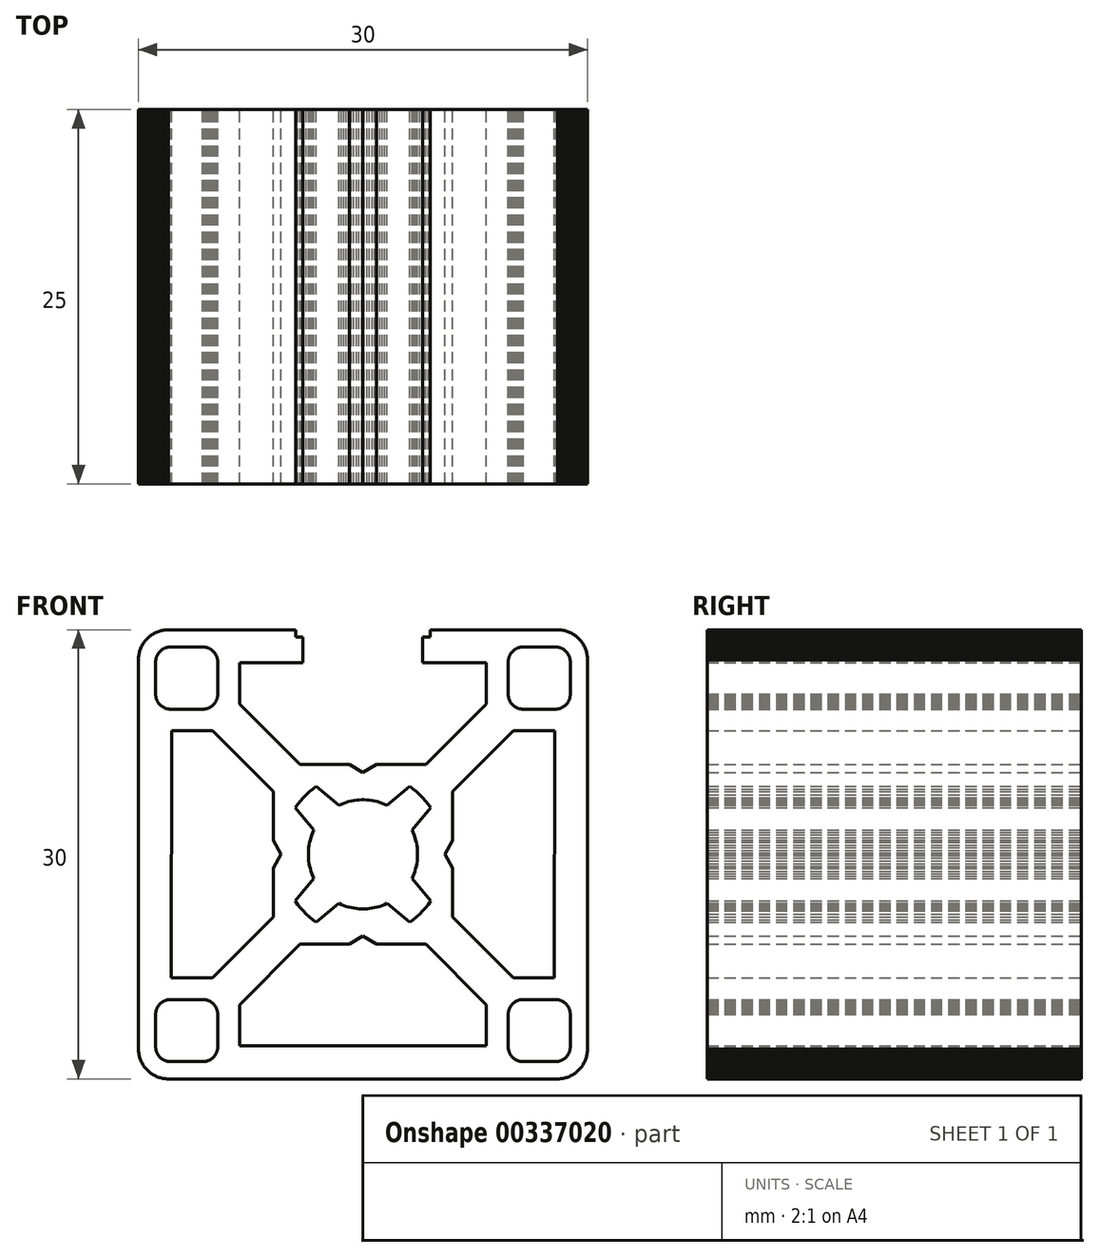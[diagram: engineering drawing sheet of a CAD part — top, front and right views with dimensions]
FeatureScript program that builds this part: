
annotation { "Feature Type Name" : "Feature", "Feature Type Description" : "" }
export const myFeature = defineFeature(function(context is Context, id is Id, definition is map)
    precondition{}
    {
        {
            var Q0;
            Q0=qCreatedBy(makeId("Front.planeOp"),FACE);
            var sketch = newSketch(context, id + "F0", { "sketchPlane" : qUnion([Q0])});
            skLineSegment(sketch, "E0", {"start": v(9.7, -12.9) * mm, "end": v(9.7, -12.85) * mm});
            skLineSegment(sketch, "E1", {"start": v(-13.85, -12.9) * mm, "end": v(-13.85, -12.85) * mm});
            skLineSegment(sketch, "E2", {"start": v(13.85, -10.7) * mm, "end": v(13.85, -10.66) * mm});
            skLineSegment(sketch, "E3", {"start": v(-9.7, -10.7) * mm, "end": v(-9.7, -10.66) * mm});
            skLineSegment(sketch, "E4", {"start": v(9.7, 10.66) * mm, "end": v(9.7, 10.7) * mm});
            skLineSegment(sketch, "E5", {"start": v(-13.85, 10.66) * mm, "end": v(-13.85, 10.7) * mm});
            skLineSegment(sketch, "E6", {"start": v(13.85, 12.85) * mm, "end": v(13.85, 12.9) * mm});
            skLineSegment(sketch, "E7", {"start": v(-9.7, 12.85) * mm, "end": v(-9.7, 12.9) * mm});
            skLineSegment(sketch, "E8", {"start": v(-15, -13.09) * mm, "end": v(-15, -13) * mm});
            skLineSegment(sketch, "E9", {"start": v(15, 13) * mm, "end": v(15, 13.09) * mm});
            skLineSegment(sketch, "E10", {"start": v(-3.64, -0.26) * mm, "end": v(-3.65, -0.09) * mm});
            skLineSegment(sketch, "E11", {"start": v(3.65, 0.09) * mm, "end": v(3.64, 0.26) * mm});
            skLineSegment(sketch, "E12", {"start": v(9.7, -12.94) * mm, "end": v(9.7, -12.9) * mm});
            skLineSegment(sketch, "E13", {"start": v(-9.7, -10.66) * mm, "end": v(-9.7, -10.61) * mm});
            skLineSegment(sketch, "E14", {"start": v(9.7, 10.61) * mm, "end": v(9.7, 10.66) * mm});
            skLineSegment(sketch, "E15", {"start": v(-9.7, 12.9) * mm, "end": v(-9.7, 12.94) * mm});
            skLineSegment(sketch, "E16", {"start": v(-15, -13.18) * mm, "end": v(-15, -13.09) * mm});
            skLineSegment(sketch, "E17", {"start": v(15, 13.09) * mm, "end": v(15, 13.18) * mm});
            skLineSegment(sketch, "E18", {"start": v(-13.85, -12.94) * mm, "end": v(-13.85, -12.9) * mm});
            skLineSegment(sketch, "E19", {"start": v(13.85, -10.66) * mm, "end": v(13.85, -10.61) * mm});
            skLineSegment(sketch, "E20", {"start": v(-13.85, 10.61) * mm, "end": v(-13.85, 10.66) * mm});
            skLineSegment(sketch, "E21", {"start": v(13.85, 12.9) * mm, "end": v(13.85, 12.94) * mm});
            skLineSegment(sketch, "E22", {"start": v(-3.62, -0.44) * mm, "end": v(-3.64, -0.26) * mm});
            skLineSegment(sketch, "E23", {"start": v(3.64, 0.26) * mm, "end": v(3.62, 0.44) * mm});
            skLineSegment(sketch, "E24", {"start": v(13.85, -10.61) * mm, "end": v(13.84, -10.57) * mm});
            skLineSegment(sketch, "E25", {"start": v(-13.84, 10.57) * mm, "end": v(-13.85, 10.61) * mm});
            skLineSegment(sketch, "E26", {"start": v(-13.84, -12.98) * mm, "end": v(-13.85, -12.94) * mm});
            skLineSegment(sketch, "E27", {"start": v(13.85, 12.94) * mm, "end": v(13.84, 12.98) * mm});
            skLineSegment(sketch, "E28", {"start": v(-14.98, -13.27) * mm, "end": v(-15, -13.18) * mm});
            skLineSegment(sketch, "E29", {"start": v(15, 13.18) * mm, "end": v(14.98, 13.27) * mm});
            skLineSegment(sketch, "E30", {"start": v(-9.7, -10.61) * mm, "end": v(-9.7, -10.57) * mm});
            skLineSegment(sketch, "E31", {"start": v(9.7, 10.57) * mm, "end": v(9.7, 10.61) * mm});
            skLineSegment(sketch, "E32", {"start": v(9.7, -12.98) * mm, "end": v(9.7, -12.94) * mm});
            skLineSegment(sketch, "E33", {"start": v(-9.7, 12.94) * mm, "end": v(-9.7, 12.98) * mm});
            skLineSegment(sketch, "E34", {"start": v(-3.6, -0.61) * mm, "end": v(-3.62, -0.44) * mm});
            skLineSegment(sketch, "E35", {"start": v(3.62, 0.44) * mm, "end": v(3.6, 0.61) * mm});
            skLineSegment(sketch, "E36", {"start": v(9.72, -13.03) * mm, "end": v(9.7, -12.98) * mm});
            skLineSegment(sketch, "E37", {"start": v(-13.83, -13.03) * mm, "end": v(-13.84, -12.98) * mm});
            skLineSegment(sketch, "E38", {"start": v(13.84, 12.98) * mm, "end": v(13.83, 13.03) * mm});
            skLineSegment(sketch, "E39", {"start": v(-9.7, 12.98) * mm, "end": v(-9.72, 13.03) * mm});
            skLineSegment(sketch, "E40", {"start": v(-14.97, -13.36) * mm, "end": v(-14.98, -13.27) * mm});
            skLineSegment(sketch, "E41", {"start": v(14.98, 13.27) * mm, "end": v(14.97, 13.36) * mm});
            skLineSegment(sketch, "E42", {"start": v(13.84, -10.57) * mm, "end": v(13.83, -10.52) * mm});
            skLineSegment(sketch, "E43", {"start": v(-9.7, -10.57) * mm, "end": v(-9.72, -10.52) * mm});
            skLineSegment(sketch, "E44", {"start": v(9.72, 10.52) * mm, "end": v(9.7, 10.57) * mm});
            skLineSegment(sketch, "E45", {"start": v(-13.83, 10.52) * mm, "end": v(-13.84, 10.57) * mm});
            skLineSegment(sketch, "E46", {"start": v(-3.56, -0.79) * mm, "end": v(-3.6, -0.61) * mm});
            skLineSegment(sketch, "E47", {"start": v(3.6, 0.61) * mm, "end": v(3.56, 0.79) * mm});
            skLineSegment(sketch, "E48", {"start": v(-14.95, -13.45) * mm, "end": v(-14.97, -13.36) * mm});
            skLineSegment(sketch, "E49", {"start": v(14.97, 13.36) * mm, "end": v(14.95, 13.45) * mm});
            skLineSegment(sketch, "E50", {"start": v(9.73, -13.07) * mm, "end": v(9.72, -13.03) * mm});
            skLineSegment(sketch, "E51", {"start": v(-13.82, -13.07) * mm, "end": v(-13.83, -13.03) * mm});
            skLineSegment(sketch, "E52", {"start": v(13.83, -10.52) * mm, "end": v(13.82, -10.48) * mm});
            skLineSegment(sketch, "E53", {"start": v(-9.72, -10.52) * mm, "end": v(-9.73, -10.48) * mm});
            skLineSegment(sketch, "E54", {"start": v(9.73, 10.48) * mm, "end": v(9.72, 10.52) * mm});
            skLineSegment(sketch, "E55", {"start": v(-13.82, 10.48) * mm, "end": v(-13.83, 10.52) * mm});
            skLineSegment(sketch, "E56", {"start": v(13.83, 13.03) * mm, "end": v(13.82, 13.07) * mm});
            skLineSegment(sketch, "E57", {"start": v(-9.72, 13.03) * mm, "end": v(-9.73, 13.07) * mm});
            skLineSegment(sketch, "E58", {"start": v(-3.52, -0.96) * mm, "end": v(-3.56, -0.79) * mm});
            skLineSegment(sketch, "E59", {"start": v(3.56, 0.79) * mm, "end": v(3.52, 0.96) * mm});
            skLineSegment(sketch, "E60", {"start": v(-14.93, -13.53) * mm, "end": v(-14.95, -13.45) * mm});
            skLineSegment(sketch, "E61", {"start": v(13.82, -10.48) * mm, "end": v(13.81, -10.43) * mm});
            skLineSegment(sketch, "E62", {"start": v(-9.73, -10.48) * mm, "end": v(-9.74, -10.43) * mm});
            skLineSegment(sketch, "E63", {"start": v(9.74, 10.43) * mm, "end": v(9.73, 10.48) * mm});
            skLineSegment(sketch, "E64", {"start": v(-13.81, 10.43) * mm, "end": v(-13.82, 10.48) * mm});
            skLineSegment(sketch, "E65", {"start": v(14.95, 13.45) * mm, "end": v(14.93, 13.53) * mm});
            skLineSegment(sketch, "E66", {"start": v(9.74, -13.12) * mm, "end": v(9.73, -13.07) * mm});
            skLineSegment(sketch, "E67", {"start": v(-13.81, -13.12) * mm, "end": v(-13.82, -13.07) * mm});
            skLineSegment(sketch, "E68", {"start": v(13.82, 13.07) * mm, "end": v(13.81, 13.12) * mm});
            skLineSegment(sketch, "E69", {"start": v(-9.73, 13.07) * mm, "end": v(-9.74, 13.12) * mm});
            skLineSegment(sketch, "E70", {"start": v(-3.47, -1.13) * mm, "end": v(-3.52, -0.96) * mm});
            skLineSegment(sketch, "E71", {"start": v(3.52, 0.96) * mm, "end": v(3.47, 1.13) * mm});
            skLineSegment(sketch, "E72", {"start": v(9.75, -13.16) * mm, "end": v(9.74, -13.12) * mm});
            skLineSegment(sketch, "E73", {"start": v(-13.8, -13.16) * mm, "end": v(-13.81, -13.12) * mm});
            skLineSegment(sketch, "E74", {"start": v(13.81, 13.12) * mm, "end": v(13.8, 13.16) * mm});
            skLineSegment(sketch, "E75", {"start": v(-9.74, 13.12) * mm, "end": v(-9.75, 13.16) * mm});
            skLineSegment(sketch, "E76", {"start": v(13.81, -10.43) * mm, "end": v(13.8, -10.4) * mm});
            skLineSegment(sketch, "E77", {"start": v(-9.74, -10.43) * mm, "end": v(-9.75, -10.4) * mm});
            skLineSegment(sketch, "E78", {"start": v(9.75, 10.4) * mm, "end": v(9.74, 10.43) * mm});
            skLineSegment(sketch, "E79", {"start": v(-13.8, 10.4) * mm, "end": v(-13.81, 10.43) * mm});
            skLineSegment(sketch, "E80", {"start": v(-14.9, -13.62) * mm, "end": v(-14.93, -13.53) * mm});
            skLineSegment(sketch, "E81", {"start": v(14.93, 13.53) * mm, "end": v(14.9, 13.62) * mm});
            skLineSegment(sketch, "E82", {"start": v(-14.87, -13.7) * mm, "end": v(-14.9, -13.62) * mm});
            skLineSegment(sketch, "E83", {"start": v(14.9, 13.62) * mm, "end": v(14.87, 13.7) * mm});
            skLineSegment(sketch, "E84", {"start": v(9.76, -13.2) * mm, "end": v(9.75, -13.16) * mm});
            skLineSegment(sketch, "E85", {"start": v(-13.79, -13.2) * mm, "end": v(-13.8, -13.16) * mm});
            skLineSegment(sketch, "E86", {"start": v(13.8, -10.4) * mm, "end": v(13.79, -10.35) * mm});
            skLineSegment(sketch, "E87", {"start": v(-9.75, -10.4) * mm, "end": v(-9.76, -10.35) * mm});
            skLineSegment(sketch, "E88", {"start": v(9.76, 10.35) * mm, "end": v(9.75, 10.4) * mm});
            skLineSegment(sketch, "E89", {"start": v(-13.79, 10.35) * mm, "end": v(-13.8, 10.4) * mm});
            skLineSegment(sketch, "E90", {"start": v(13.8, 13.16) * mm, "end": v(13.79, 13.2) * mm});
            skLineSegment(sketch, "E91", {"start": v(-9.75, 13.16) * mm, "end": v(-9.76, 13.2) * mm});
            skLineSegment(sketch, "E92", {"start": v(-3.41, -1.3) * mm, "end": v(-3.47, -1.13) * mm});
            skLineSegment(sketch, "E93", {"start": v(3.47, 1.13) * mm, "end": v(3.41, 1.3) * mm});
            skLineSegment(sketch, "E94", {"start": v(-14.84, -13.79) * mm, "end": v(-14.87, -13.7) * mm});
            skLineSegment(sketch, "E95", {"start": v(14.87, 13.7) * mm, "end": v(14.84, 13.79) * mm});
            skLineSegment(sketch, "E96", {"start": v(9.78, -13.24) * mm, "end": v(9.76, -13.2) * mm});
            skLineSegment(sketch, "E97", {"start": v(-9.76, -10.35) * mm, "end": v(-9.78, -10.3) * mm});
            skLineSegment(sketch, "E98", {"start": v(9.78, 10.3) * mm, "end": v(9.76, 10.35) * mm});
            skLineSegment(sketch, "E99", {"start": v(-9.76, 13.2) * mm, "end": v(-9.78, 13.24) * mm});
            skLineSegment(sketch, "E100", {"start": v(-13.77, -13.24) * mm, "end": v(-13.79, -13.2) * mm});
            skLineSegment(sketch, "E101", {"start": v(13.79, -10.35) * mm, "end": v(13.77, -10.3) * mm});
            skLineSegment(sketch, "E102", {"start": v(-13.77, 10.3) * mm, "end": v(-13.79, 10.35) * mm});
            skLineSegment(sketch, "E103", {"start": v(13.79, 13.2) * mm, "end": v(13.77, 13.24) * mm});
            skLineSegment(sketch, "E104", {"start": v(-3.35, -1.46) * mm, "end": v(-3.41, -1.3) * mm});
            skLineSegment(sketch, "E105", {"start": v(3.41, 1.3) * mm, "end": v(3.35, 1.46) * mm});
            skLineSegment(sketch, "E106", {"start": v(-13.75, -13.28) * mm, "end": v(-13.77, -13.24) * mm});
            skLineSegment(sketch, "E107", {"start": v(13.77, -10.3) * mm, "end": v(13.75, -10.27) * mm});
            skLineSegment(sketch, "E108", {"start": v(-13.75, 10.27) * mm, "end": v(-13.77, 10.3) * mm});
            skLineSegment(sketch, "E109", {"start": v(13.77, 13.24) * mm, "end": v(13.75, 13.28) * mm});
            skLineSegment(sketch, "E110", {"start": v(9.8, -13.28) * mm, "end": v(9.78, -13.24) * mm});
            skLineSegment(sketch, "E111", {"start": v(-9.78, -10.3) * mm, "end": v(-9.8, -10.27) * mm});
            skLineSegment(sketch, "E112", {"start": v(9.8, 10.27) * mm, "end": v(9.78, 10.3) * mm});
            skLineSegment(sketch, "E113", {"start": v(-9.78, 13.24) * mm, "end": v(-9.8, 13.28) * mm});
            skLineSegment(sketch, "E114", {"start": v(-14.8, -13.87) * mm, "end": v(-14.84, -13.79) * mm});
            skLineSegment(sketch, "E115", {"start": v(14.84, 13.79) * mm, "end": v(14.8, 13.87) * mm});
            skLineSegment(sketch, "E116", {"start": v(-3.27, -1.62) * mm, "end": v(-3.35, -1.46) * mm});
            skLineSegment(sketch, "E117", {"start": v(3.35, 1.46) * mm, "end": v(3.27, 1.62) * mm});
            skLineSegment(sketch, "E118", {"start": v(-13.73, -13.32) * mm, "end": v(-13.75, -13.28) * mm});
            skLineSegment(sketch, "E119", {"start": v(13.75, -10.27) * mm, "end": v(13.73, -10.23) * mm});
            skLineSegment(sketch, "E120", {"start": v(-13.73, 10.23) * mm, "end": v(-13.75, 10.27) * mm});
            skLineSegment(sketch, "E121", {"start": v(13.75, 13.28) * mm, "end": v(13.73, 13.32) * mm});
            skLineSegment(sketch, "E122", {"start": v(-14.76, -13.95) * mm, "end": v(-14.8, -13.87) * mm});
            skLineSegment(sketch, "E123", {"start": v(14.8, 13.87) * mm, "end": v(14.76, 13.95) * mm});
            skLineSegment(sketch, "E124", {"start": v(9.82, -13.32) * mm, "end": v(9.8, -13.28) * mm});
            skLineSegment(sketch, "E125", {"start": v(-9.8, -10.27) * mm, "end": v(-9.82, -10.23) * mm});
            skLineSegment(sketch, "E126", {"start": v(9.82, 10.23) * mm, "end": v(9.8, 10.27) * mm});
            skLineSegment(sketch, "E127", {"start": v(-9.8, 13.28) * mm, "end": v(-9.82, 13.32) * mm});
            skLineSegment(sketch, "E128", {"start": v(-9.82, -10.23) * mm, "end": v(-9.84, -10.19) * mm});
            skLineSegment(sketch, "E129", {"start": v(9.84, 10.19) * mm, "end": v(9.82, 10.23) * mm});
            skLineSegment(sketch, "E130", {"start": v(9.84, -13.36) * mm, "end": v(9.82, -13.32) * mm});
            skLineSegment(sketch, "E131", {"start": v(-9.82, 13.32) * mm, "end": v(-9.84, 13.36) * mm});
            skLineSegment(sketch, "E132", {"start": v(-14.72, -14.03) * mm, "end": v(-14.76, -13.95) * mm});
            skLineSegment(sketch, "E133", {"start": v(14.76, 13.95) * mm, "end": v(14.72, 14.03) * mm});
            skLineSegment(sketch, "E134", {"start": v(13.73, -10.23) * mm, "end": v(13.7, -10.19) * mm});
            skLineSegment(sketch, "E135", {"start": v(-13.7, 10.19) * mm, "end": v(-13.73, 10.23) * mm});
            skLineSegment(sketch, "E136", {"start": v(-13.7, -13.36) * mm, "end": v(-13.73, -13.32) * mm});
            skLineSegment(sketch, "E137", {"start": v(13.73, 13.32) * mm, "end": v(13.7, 13.36) * mm});
            skLineSegment(sketch, "E138", {"start": v(6, -0.92) * mm, "end": v(5.47, 0) * mm});
            skLineSegment(sketch, "E139", {"start": v(-5.47, 0) * mm, "end": v(-6, 0.92) * mm});
            skLineSegment(sketch, "E140", {"start": v(-13.68, -13.4) * mm, "end": v(-13.7, -13.36) * mm});
            skLineSegment(sketch, "E141", {"start": v(13.7, 13.36) * mm, "end": v(13.68, 13.4) * mm});
            skLineSegment(sketch, "E142", {"start": v(13.7, -10.19) * mm, "end": v(13.68, -10.15) * mm});
            skLineSegment(sketch, "E143", {"start": v(-13.68, 10.15) * mm, "end": v(-13.7, 10.19) * mm});
            skLineSegment(sketch, "E144", {"start": v(-14.67, -14.1) * mm, "end": v(-14.72, -14.03) * mm});
            skLineSegment(sketch, "E145", {"start": v(14.72, 14.03) * mm, "end": v(14.67, 14.1) * mm});
            skLineSegment(sketch, "E146", {"start": v(9.87, -13.4) * mm, "end": v(9.84, -13.36) * mm});
            skLineSegment(sketch, "E147", {"start": v(-9.84, 13.36) * mm, "end": v(-9.87, 13.4) * mm});
            skLineSegment(sketch, "E148", {"start": v(-9.84, -10.19) * mm, "end": v(-9.87, -10.15) * mm});
            skLineSegment(sketch, "E149", {"start": v(9.87, 10.15) * mm, "end": v(9.84, 10.19) * mm});
            skLineSegment(sketch, "E150", {"start": v(9.9, -13.44) * mm, "end": v(9.87, -13.4) * mm});
            skLineSegment(sketch, "E151", {"start": v(-13.66, -13.44) * mm, "end": v(-13.68, -13.4) * mm});
            skLineSegment(sketch, "E152", {"start": v(13.68, -10.15) * mm, "end": v(13.66, -10.11) * mm});
            skLineSegment(sketch, "E153", {"start": v(-9.87, -10.15) * mm, "end": v(-9.9, -10.11) * mm});
            skLineSegment(sketch, "E154", {"start": v(9.9, 10.11) * mm, "end": v(9.87, 10.15) * mm});
            skLineSegment(sketch, "E155", {"start": v(-13.66, 10.11) * mm, "end": v(-13.68, 10.15) * mm});
            skLineSegment(sketch, "E156", {"start": v(13.68, 13.4) * mm, "end": v(13.66, 13.44) * mm});
            skLineSegment(sketch, "E157", {"start": v(-9.87, 13.4) * mm, "end": v(-9.9, 13.44) * mm});
            skLineSegment(sketch, "E158", {"start": v(-14.62, -14.18) * mm, "end": v(-14.67, -14.1) * mm});
            skLineSegment(sketch, "E159", {"start": v(14.67, 14.1) * mm, "end": v(14.62, 14.18) * mm});
            skLineSegment(sketch, "E160", {"start": v(-4.36, -3.35) * mm, "end": v(-4.53, -3.12) * mm});
            skLineSegment(sketch, "E161", {"start": v(4.53, 3.12) * mm, "end": v(4.36, 3.35) * mm});
            skLineSegment(sketch, "E162", {"start": v(9.92, -13.47) * mm, "end": v(9.9, -13.44) * mm});
            skLineSegment(sketch, "E163", {"start": v(-9.9, -10.11) * mm, "end": v(-9.92, -10.08) * mm});
            skLineSegment(sketch, "E164", {"start": v(9.92, 10.08) * mm, "end": v(9.9, 10.11) * mm});
            skLineSegment(sketch, "E165", {"start": v(-9.9, 13.44) * mm, "end": v(-9.92, 13.47) * mm});
            skLineSegment(sketch, "E166", {"start": v(-14.56, -14.25) * mm, "end": v(-14.62, -14.18) * mm});
            skLineSegment(sketch, "E167", {"start": v(14.62, 14.18) * mm, "end": v(14.56, 14.25) * mm});
            skLineSegment(sketch, "E168", {"start": v(-13.63, -13.47) * mm, "end": v(-13.66, -13.44) * mm});
            skLineSegment(sketch, "E169", {"start": v(13.66, -10.11) * mm, "end": v(13.63, -10.08) * mm});
            skLineSegment(sketch, "E170", {"start": v(-13.63, 10.08) * mm, "end": v(-13.66, 10.11) * mm});
            skLineSegment(sketch, "E171", {"start": v(13.66, 13.44) * mm, "end": v(13.63, 13.47) * mm});
            skLineSegment(sketch, "E172", {"start": v(-4.18, -3.57) * mm, "end": v(-4.36, -3.35) * mm});
            skLineSegment(sketch, "E173", {"start": v(4.36, 3.35) * mm, "end": v(4.18, 3.57) * mm});
            skLineSegment(sketch, "E174", {"start": v(-14.5, -14.32) * mm, "end": v(-14.56, -14.25) * mm});
            skLineSegment(sketch, "E175", {"start": v(13.63, -10.08) * mm, "end": v(13.6, -10.04) * mm});
            skLineSegment(sketch, "E176", {"start": v(-13.6, 10.04) * mm, "end": v(-13.63, 10.08) * mm});
            skLineSegment(sketch, "E177", {"start": v(14.56, 14.25) * mm, "end": v(14.5, 14.32) * mm});
            skLineSegment(sketch, "E178", {"start": v(-13.6, -13.5) * mm, "end": v(-13.63, -13.47) * mm});
            skLineSegment(sketch, "E179", {"start": v(13.63, 13.47) * mm, "end": v(13.6, 13.5) * mm});
            skLineSegment(sketch, "E180", {"start": v(-9.92, -10.08) * mm, "end": v(-9.95, -10.04) * mm});
            skLineSegment(sketch, "E181", {"start": v(9.95, 10.04) * mm, "end": v(9.92, 10.08) * mm});
            skLineSegment(sketch, "E182", {"start": v(9.95, -13.5) * mm, "end": v(9.92, -13.47) * mm});
            skLineSegment(sketch, "E183", {"start": v(-9.92, 13.47) * mm, "end": v(-9.95, 13.5) * mm});
            skLineSegment(sketch, "E184", {"start": v(4.53, -3.12) * mm, "end": v(3.27, -1.62) * mm});
            skLineSegment(sketch, "E185", {"start": v(-3.27, 1.62) * mm, "end": v(-4.53, 3.12) * mm});
            skLineSegment(sketch, "E186", {"start": v(-3.99, -3.79) * mm, "end": v(-4.18, -3.57) * mm});
            skLineSegment(sketch, "E187", {"start": v(4.18, 3.57) * mm, "end": v(3.99, 3.79) * mm});
            skLineSegment(sketch, "E188", {"start": v(9.98, -13.54) * mm, "end": v(9.95, -13.5) * mm});
            skLineSegment(sketch, "E189", {"start": v(-13.57, -13.54) * mm, "end": v(-13.6, -13.5) * mm});
            skLineSegment(sketch, "E190", {"start": v(13.6, -10.04) * mm, "end": v(13.57, -10) * mm});
            skLineSegment(sketch, "E191", {"start": v(-9.95, -10.04) * mm, "end": v(-9.98, -10) * mm});
            skLineSegment(sketch, "E192", {"start": v(9.98, 10) * mm, "end": v(9.95, 10.04) * mm});
            skLineSegment(sketch, "E193", {"start": v(-13.57, 10) * mm, "end": v(-13.6, 10.04) * mm});
            skLineSegment(sketch, "E194", {"start": v(13.6, 13.5) * mm, "end": v(13.57, 13.54) * mm});
            skLineSegment(sketch, "E195", {"start": v(-9.95, 13.5) * mm, "end": v(-9.98, 13.54) * mm});
            skLineSegment(sketch, "E196", {"start": v(-14.45, -14.38) * mm, "end": v(-14.5, -14.32) * mm});
            skLineSegment(sketch, "E197", {"start": v(14.5, 14.32) * mm, "end": v(14.45, 14.38) * mm});
            skLineSegment(sketch, "E198", {"start": v(10, -13.57) * mm, "end": v(9.98, -13.54) * mm});
            skLineSegment(sketch, "E199", {"start": v(-9.98, 13.54) * mm, "end": v(-10, 13.57) * mm});
            skLineSegment(sketch, "E200", {"start": v(-14.38, -14.45) * mm, "end": v(-14.45, -14.38) * mm});
            skLineSegment(sketch, "E201", {"start": v(-13.54, -13.57) * mm, "end": v(-13.57, -13.54) * mm});
            skLineSegment(sketch, "E202", {"start": v(8.25, -10.05) * mm, "end": v(4.2, -6) * mm});
            skLineSegment(sketch, "E203", {"start": v(-9.98, -10) * mm, "end": v(-10, -9.98) * mm});
            skLineSegment(sketch, "E204", {"start": v(-3.79, -3.99) * mm, "end": v(-3.99, -3.79) * mm});
            skLineSegment(sketch, "E205", {"start": v(3.99, 3.79) * mm, "end": v(3.79, 3.99) * mm});
            skLineSegment(sketch, "E206", {"start": v(-6, 4.2) * mm, "end": v(-10.05, 8.25) * mm});
            skLineSegment(sketch, "E207", {"start": v(-4.2, 6) * mm, "end": v(-8.25, 10.05) * mm});
            skLineSegment(sketch, "E208", {"start": v(10.05, -8.25) * mm, "end": v(6, -4.2) * mm});
            skLineSegment(sketch, "E209", {"start": v(10, 9.98) * mm, "end": v(9.98, 10) * mm});
            skLineSegment(sketch, "E210", {"start": v(13.57, 13.54) * mm, "end": v(13.54, 13.57) * mm});
            skLineSegment(sketch, "E211", {"start": v(14.45, 14.38) * mm, "end": v(14.38, 14.45) * mm});
            skLineSegment(sketch, "E212", {"start": v(13.57, -10) * mm, "end": v(13.54, -9.98) * mm});
            skLineSegment(sketch, "E213", {"start": v(-13.54, 9.98) * mm, "end": v(-13.57, 10) * mm});
            skLineSegment(sketch, "E214", {"start": v(-14.32, -14.5) * mm, "end": v(-14.38, -14.45) * mm});
            skLineSegment(sketch, "E215", {"start": v(14.38, 14.45) * mm, "end": v(14.32, 14.5) * mm});
            skLineSegment(sketch, "E216", {"start": v(10.04, -13.6) * mm, "end": v(10, -13.57) * mm});
            skLineSegment(sketch, "E217", {"start": v(-13.5, -13.6) * mm, "end": v(-13.54, -13.57) * mm});
            skLineSegment(sketch, "E218", {"start": v(13.54, -9.98) * mm, "end": v(13.5, -9.95) * mm});
            skLineSegment(sketch, "E219", {"start": v(-10, -9.98) * mm, "end": v(-10.04, -9.95) * mm});
            skLineSegment(sketch, "E220", {"start": v(10.04, 9.95) * mm, "end": v(10, 9.98) * mm});
            skLineSegment(sketch, "E221", {"start": v(-13.5, 9.95) * mm, "end": v(-13.54, 9.98) * mm});
            skLineSegment(sketch, "E222", {"start": v(13.54, 13.57) * mm, "end": v(13.5, 13.6) * mm});
            skLineSegment(sketch, "E223", {"start": v(-10, 13.57) * mm, "end": v(-10.04, 13.6) * mm});
            skLineSegment(sketch, "E224", {"start": v(-3.57, -4.18) * mm, "end": v(-3.79, -3.99) * mm});
            skLineSegment(sketch, "E225", {"start": v(3.79, 3.99) * mm, "end": v(3.57, 4.18) * mm});
            skLineSegment(sketch, "E226", {"start": v(3.12, -4.53) * mm, "end": v(1.62, -3.27) * mm});
            skLineSegment(sketch, "E227", {"start": v(-1.62, 3.27) * mm, "end": v(-3.12, 4.53) * mm});
            skLineSegment(sketch, "E228", {"start": v(13.5, -9.95) * mm, "end": v(13.47, -9.92) * mm});
            skLineSegment(sketch, "E229", {"start": v(-13.47, 9.92) * mm, "end": v(-13.5, 9.95) * mm});
            skLineSegment(sketch, "E230", {"start": v(-10.04, -9.95) * mm, "end": v(-10.08, -9.92) * mm});
            skLineSegment(sketch, "E231", {"start": v(10.08, 9.92) * mm, "end": v(10.04, 9.95) * mm});
            skLineSegment(sketch, "E232", {"start": v(-13.47, -13.63) * mm, "end": v(-13.5, -13.6) * mm});
            skLineSegment(sketch, "E233", {"start": v(13.5, 13.6) * mm, "end": v(13.47, 13.63) * mm});
            skLineSegment(sketch, "E234", {"start": v(-14.25, -14.56) * mm, "end": v(-14.32, -14.5) * mm});
            skLineSegment(sketch, "E235", {"start": v(10.08, -13.63) * mm, "end": v(10.04, -13.6) * mm});
            skLineSegment(sketch, "E236", {"start": v(-10.04, 13.6) * mm, "end": v(-10.08, 13.63) * mm});
            skLineSegment(sketch, "E237", {"start": v(14.32, 14.5) * mm, "end": v(14.25, 14.56) * mm});
            skLineSegment(sketch, "E238", {"start": v(-3.35, -4.36) * mm, "end": v(-3.57, -4.18) * mm});
            skLineSegment(sketch, "E239", {"start": v(3.57, 4.18) * mm, "end": v(3.35, 4.36) * mm});
            skLineSegment(sketch, "E240", {"start": v(10.11, -13.66) * mm, "end": v(10.08, -13.63) * mm});
            skLineSegment(sketch, "E241", {"start": v(-13.44, -13.66) * mm, "end": v(-13.47, -13.63) * mm});
            skLineSegment(sketch, "E242", {"start": v(13.47, 13.63) * mm, "end": v(13.44, 13.66) * mm});
            skLineSegment(sketch, "E243", {"start": v(-10.08, 13.63) * mm, "end": v(-10.11, 13.66) * mm});
            skLineSegment(sketch, "E244", {"start": v(-14.18, -14.62) * mm, "end": v(-14.25, -14.56) * mm});
            skLineSegment(sketch, "E245", {"start": v(14.25, 14.56) * mm, "end": v(14.18, 14.62) * mm});
            skLineSegment(sketch, "E246", {"start": v(13.47, -9.92) * mm, "end": v(13.44, -9.9) * mm});
            skLineSegment(sketch, "E247", {"start": v(-10.08, -9.92) * mm, "end": v(-10.11, -9.9) * mm});
            skLineSegment(sketch, "E248", {"start": v(10.11, 9.9) * mm, "end": v(10.08, 9.92) * mm});
            skLineSegment(sketch, "E249", {"start": v(-13.44, 9.9) * mm, "end": v(-13.47, 9.92) * mm});
            skLineSegment(sketch, "E250", {"start": v(-3.12, -4.53) * mm, "end": v(-3.35, -4.36) * mm});
            skLineSegment(sketch, "E251", {"start": v(3.35, 4.36) * mm, "end": v(3.12, 4.53) * mm});
            skLineSegment(sketch, "E252", {"start": v(-14.1, -14.67) * mm, "end": v(-14.18, -14.62) * mm});
            skLineSegment(sketch, "E253", {"start": v(14.18, 14.62) * mm, "end": v(14.1, 14.67) * mm});
            skLineSegment(sketch, "E254", {"start": v(10.15, -13.68) * mm, "end": v(10.11, -13.66) * mm});
            skLineSegment(sketch, "E255", {"start": v(-13.4, -13.68) * mm, "end": v(-13.44, -13.66) * mm});
            skLineSegment(sketch, "E256", {"start": v(13.44, -9.9) * mm, "end": v(13.4, -9.87) * mm});
            skLineSegment(sketch, "E257", {"start": v(-10.11, -9.9) * mm, "end": v(-10.15, -9.87) * mm});
            skLineSegment(sketch, "E258", {"start": v(10.15, 9.87) * mm, "end": v(10.11, 9.9) * mm});
            skLineSegment(sketch, "E259", {"start": v(-13.4, 9.87) * mm, "end": v(-13.44, 9.9) * mm});
            skLineSegment(sketch, "E260", {"start": v(13.44, 13.66) * mm, "end": v(13.4, 13.68) * mm});
            skLineSegment(sketch, "E261", {"start": v(-10.11, 13.66) * mm, "end": v(-10.15, 13.68) * mm});
            skLineSegment(sketch, "E262", {"start": v(-10.15, -9.87) * mm, "end": v(-10.19, -9.84) * mm});
            skLineSegment(sketch, "E263", {"start": v(10.19, 9.84) * mm, "end": v(10.15, 9.87) * mm});
            skLineSegment(sketch, "E264", {"start": v(13.4, -9.87) * mm, "end": v(13.36, -9.84) * mm});
            skLineSegment(sketch, "E265", {"start": v(-13.36, 9.84) * mm, "end": v(-13.4, 9.87) * mm});
            skLineSegment(sketch, "E266", {"start": v(-14.03, -14.72) * mm, "end": v(-14.1, -14.67) * mm});
            skLineSegment(sketch, "E267", {"start": v(14.1, 14.67) * mm, "end": v(14.03, 14.72) * mm});
            skLineSegment(sketch, "E268", {"start": v(10.19, -13.7) * mm, "end": v(10.15, -13.68) * mm});
            skLineSegment(sketch, "E269", {"start": v(-10.15, 13.68) * mm, "end": v(-10.19, 13.7) * mm});
            skLineSegment(sketch, "E270", {"start": v(-13.36, -13.7) * mm, "end": v(-13.4, -13.68) * mm});
            skLineSegment(sketch, "E271", {"start": v(13.4, 13.68) * mm, "end": v(13.36, 13.7) * mm});
            skLineSegment(sketch, "E272", {"start": v(0.92, -6) * mm, "end": v(0, -5.47) * mm});
            skLineSegment(sketch, "E273", {"start": v(0, 5.47) * mm, "end": v(-0.92, 6) * mm});
            skLineSegment(sketch, "E274", {"start": v(-13.32, -13.73) * mm, "end": v(-13.36, -13.7) * mm});
            skLineSegment(sketch, "E275", {"start": v(13.36, 13.7) * mm, "end": v(13.32, 13.73) * mm});
            skLineSegment(sketch, "E276", {"start": v(10.23, -13.73) * mm, "end": v(10.19, -13.7) * mm});
            skLineSegment(sketch, "E277", {"start": v(-10.19, 13.7) * mm, "end": v(-10.23, 13.73) * mm});
            skLineSegment(sketch, "E278", {"start": v(-13.95, -14.76) * mm, "end": v(-14.03, -14.72) * mm});
            skLineSegment(sketch, "E279", {"start": v(14.03, 14.72) * mm, "end": v(13.95, 14.76) * mm});
            skLineSegment(sketch, "E280", {"start": v(13.36, -9.84) * mm, "end": v(13.32, -9.82) * mm});
            skLineSegment(sketch, "E281", {"start": v(-13.32, 9.82) * mm, "end": v(-13.36, 9.84) * mm});
            skLineSegment(sketch, "E282", {"start": v(-10.19, -9.84) * mm, "end": v(-10.23, -9.82) * mm});
            skLineSegment(sketch, "E283", {"start": v(10.23, 9.82) * mm, "end": v(10.19, 9.84) * mm});
            skLineSegment(sketch, "E284", {"start": v(13.32, -9.82) * mm, "end": v(13.28, -9.8) * mm});
            skLineSegment(sketch, "E285", {"start": v(-10.23, -9.82) * mm, "end": v(-10.27, -9.8) * mm});
            skLineSegment(sketch, "E286", {"start": v(10.27, 9.8) * mm, "end": v(10.23, 9.82) * mm});
            skLineSegment(sketch, "E287", {"start": v(-13.28, 9.8) * mm, "end": v(-13.32, 9.82) * mm});
            skLineSegment(sketch, "E288", {"start": v(-13.87, -14.8) * mm, "end": v(-13.95, -14.76) * mm});
            skLineSegment(sketch, "E289", {"start": v(13.95, 14.76) * mm, "end": v(13.87, 14.8) * mm});
            skLineSegment(sketch, "E290", {"start": v(10.27, -13.75) * mm, "end": v(10.23, -13.73) * mm});
            skLineSegment(sketch, "E291", {"start": v(-13.28, -13.75) * mm, "end": v(-13.32, -13.73) * mm});
            skLineSegment(sketch, "E292", {"start": v(13.32, 13.73) * mm, "end": v(13.28, 13.75) * mm});
            skLineSegment(sketch, "E293", {"start": v(-10.23, 13.73) * mm, "end": v(-10.27, 13.75) * mm});
            skLineSegment(sketch, "E294", {"start": v(-1.46, -3.35) * mm, "end": v(-1.62, -3.27) * mm});
            skLineSegment(sketch, "E295", {"start": v(1.62, 3.27) * mm, "end": v(1.46, 3.35) * mm});
            skLineSegment(sketch, "E296", {"start": v(-13.79, -14.84) * mm, "end": v(-13.87, -14.8) * mm});
            skLineSegment(sketch, "E297", {"start": v(13.87, 14.8) * mm, "end": v(13.79, 14.84) * mm});
            skLineSegment(sketch, "E298", {"start": v(13.28, -9.8) * mm, "end": v(13.24, -9.78) * mm});
            skLineSegment(sketch, "E299", {"start": v(-10.27, -9.8) * mm, "end": v(-10.3, -9.78) * mm});
            skLineSegment(sketch, "E300", {"start": v(10.3, 9.78) * mm, "end": v(10.27, 9.8) * mm});
            skLineSegment(sketch, "E301", {"start": v(-13.24, 9.78) * mm, "end": v(-13.28, 9.8) * mm});
            skLineSegment(sketch, "E302", {"start": v(10.3, -13.77) * mm, "end": v(10.27, -13.75) * mm});
            skLineSegment(sketch, "E303", {"start": v(-13.24, -13.77) * mm, "end": v(-13.28, -13.75) * mm});
            skLineSegment(sketch, "E304", {"start": v(13.28, 13.75) * mm, "end": v(13.24, 13.77) * mm});
            skLineSegment(sketch, "E305", {"start": v(-10.27, 13.75) * mm, "end": v(-10.3, 13.77) * mm});
            skLineSegment(sketch, "E306", {"start": v(-1.3, -3.41) * mm, "end": v(-1.46, -3.35) * mm});
            skLineSegment(sketch, "E307", {"start": v(1.46, 3.35) * mm, "end": v(1.3, 3.41) * mm});
            skLineSegment(sketch, "E308", {"start": v(10.35, -13.79) * mm, "end": v(10.3, -13.77) * mm});
            skLineSegment(sketch, "E309", {"start": v(-13.2, -13.79) * mm, "end": v(-13.24, -13.77) * mm});
            skLineSegment(sketch, "E310", {"start": v(13.24, 13.77) * mm, "end": v(13.2, 13.79) * mm});
            skLineSegment(sketch, "E311", {"start": v(-10.3, 13.77) * mm, "end": v(-10.35, 13.79) * mm});
            skLineSegment(sketch, "E312", {"start": v(13.24, -9.78) * mm, "end": v(13.2, -9.76) * mm});
            skLineSegment(sketch, "E313", {"start": v(-10.3, -9.78) * mm, "end": v(-10.35, -9.76) * mm});
            skLineSegment(sketch, "E314", {"start": v(10.35, 9.76) * mm, "end": v(10.3, 9.78) * mm});
            skLineSegment(sketch, "E315", {"start": v(-13.2, 9.76) * mm, "end": v(-13.24, 9.78) * mm});
            skLineSegment(sketch, "E316", {"start": v(-13.7, -14.87) * mm, "end": v(-13.79, -14.84) * mm});
            skLineSegment(sketch, "E317", {"start": v(13.79, 14.84) * mm, "end": v(13.7, 14.87) * mm});
            skLineSegment(sketch, "E318", {"start": v(-1.13, -3.47) * mm, "end": v(-1.3, -3.41) * mm});
            skLineSegment(sketch, "E319", {"start": v(1.3, 3.41) * mm, "end": v(1.13, 3.47) * mm});
            skLineSegment(sketch, "E320", {"start": v(10.4, -13.8) * mm, "end": v(10.35, -13.79) * mm});
            skLineSegment(sketch, "E321", {"start": v(-13.16, -13.8) * mm, "end": v(-13.2, -13.79) * mm});
            skLineSegment(sketch, "E322", {"start": v(13.2, -9.76) * mm, "end": v(13.16, -9.75) * mm});
            skLineSegment(sketch, "E323", {"start": v(-10.35, -9.76) * mm, "end": v(-10.4, -9.75) * mm});
            skLineSegment(sketch, "E324", {"start": v(10.4, 9.75) * mm, "end": v(10.35, 9.76) * mm});
            skLineSegment(sketch, "E325", {"start": v(-13.16, 9.75) * mm, "end": v(-13.2, 9.76) * mm});
            skLineSegment(sketch, "E326", {"start": v(13.2, 13.79) * mm, "end": v(13.16, 13.8) * mm});
            skLineSegment(sketch, "E327", {"start": v(-10.35, 13.79) * mm, "end": v(-10.4, 13.8) * mm});
            skLineSegment(sketch, "E328", {"start": v(-13.62, -14.9) * mm, "end": v(-13.7, -14.87) * mm});
            skLineSegment(sketch, "E329", {"start": v(13.7, 14.87) * mm, "end": v(13.62, 14.9) * mm});
            skLineSegment(sketch, "E330", {"start": v(-13.53, -14.93) * mm, "end": v(-13.62, -14.9) * mm});
            skLineSegment(sketch, "E331", {"start": v(13.62, 14.9) * mm, "end": v(13.53, 14.93) * mm});
            skLineSegment(sketch, "E332", {"start": v(10.43, -13.81) * mm, "end": v(10.4, -13.8) * mm});
            skLineSegment(sketch, "E333", {"start": v(-10.4, -9.75) * mm, "end": v(-10.43, -9.74) * mm});
            skLineSegment(sketch, "E334", {"start": v(10.43, 9.74) * mm, "end": v(10.4, 9.75) * mm});
            skLineSegment(sketch, "E335", {"start": v(-10.4, 13.8) * mm, "end": v(-10.43, 13.81) * mm});
            skLineSegment(sketch, "E336", {"start": v(-13.12, -13.81) * mm, "end": v(-13.16, -13.8) * mm});
            skLineSegment(sketch, "E337", {"start": v(13.16, -9.75) * mm, "end": v(13.12, -9.74) * mm});
            skLineSegment(sketch, "E338", {"start": v(-13.12, 9.74) * mm, "end": v(-13.16, 9.75) * mm});
            skLineSegment(sketch, "E339", {"start": v(13.16, 13.8) * mm, "end": v(13.12, 13.81) * mm});
            skLineSegment(sketch, "E340", {"start": v(-0.96, -3.52) * mm, "end": v(-1.13, -3.47) * mm});
            skLineSegment(sketch, "E341", {"start": v(1.13, 3.47) * mm, "end": v(0.96, 3.52) * mm});
            skLineSegment(sketch, "E342", {"start": v(-13.07, -13.82) * mm, "end": v(-13.12, -13.81) * mm});
            skLineSegment(sketch, "E343", {"start": v(13.12, -9.74) * mm, "end": v(13.07, -9.73) * mm});
            skLineSegment(sketch, "E344", {"start": v(-13.07, 9.73) * mm, "end": v(-13.12, 9.74) * mm});
            skLineSegment(sketch, "E345", {"start": v(13.12, 13.81) * mm, "end": v(13.07, 13.82) * mm});
            skLineSegment(sketch, "E346", {"start": v(-13.45, -14.95) * mm, "end": v(-13.53, -14.93) * mm});
            skLineSegment(sketch, "E347", {"start": v(10.48, -13.82) * mm, "end": v(10.43, -13.81) * mm});
            skLineSegment(sketch, "E348", {"start": v(-10.43, -9.74) * mm, "end": v(-10.48, -9.73) * mm});
            skLineSegment(sketch, "E349", {"start": v(10.48, 9.73) * mm, "end": v(10.43, 9.74) * mm});
            skLineSegment(sketch, "E350", {"start": v(-10.43, 13.81) * mm, "end": v(-10.48, 13.82) * mm});
            skLineSegment(sketch, "E351", {"start": v(13.53, 14.93) * mm, "end": v(13.45, 14.95) * mm});
            skLineSegment(sketch, "E352", {"start": v(-0.79, -3.56) * mm, "end": v(-0.96, -3.52) * mm});
            skLineSegment(sketch, "E353", {"start": v(0.96, 3.52) * mm, "end": v(0.79, 3.56) * mm});
            skLineSegment(sketch, "E354", {"start": v(10.52, -13.83) * mm, "end": v(10.48, -13.82) * mm});
            skLineSegment(sketch, "E355", {"start": v(-13.03, -13.83) * mm, "end": v(-13.07, -13.82) * mm});
            skLineSegment(sketch, "E356", {"start": v(13.07, -9.73) * mm, "end": v(13.03, -9.72) * mm});
            skLineSegment(sketch, "E357", {"start": v(-10.48, -9.73) * mm, "end": v(-10.52, -9.72) * mm});
            skLineSegment(sketch, "E358", {"start": v(10.52, 9.72) * mm, "end": v(10.48, 9.73) * mm});
            skLineSegment(sketch, "E359", {"start": v(-13.03, 9.72) * mm, "end": v(-13.07, 9.73) * mm});
            skLineSegment(sketch, "E360", {"start": v(13.07, 13.82) * mm, "end": v(13.03, 13.83) * mm});
            skLineSegment(sketch, "E361", {"start": v(-10.48, 13.82) * mm, "end": v(-10.52, 13.83) * mm});
            skLineSegment(sketch, "E362", {"start": v(-13.36, -14.97) * mm, "end": v(-13.45, -14.95) * mm});
            skLineSegment(sketch, "E363", {"start": v(13.45, 14.95) * mm, "end": v(13.36, 14.97) * mm});
            skLineSegment(sketch, "E364", {"start": v(-0.61, -3.6) * mm, "end": v(-0.79, -3.56) * mm});
            skLineSegment(sketch, "E365", {"start": v(0.79, 3.56) * mm, "end": v(0.61, 3.6) * mm});
            skLineSegment(sketch, "E366", {"start": v(10.57, -13.84) * mm, "end": v(10.52, -13.83) * mm});
            skLineSegment(sketch, "E367", {"start": v(-10.52, -9.72) * mm, "end": v(-10.57, -9.7) * mm});
            skLineSegment(sketch, "E368", {"start": v(10.57, 9.7) * mm, "end": v(10.52, 9.72) * mm});
            skLineSegment(sketch, "E369", {"start": v(-10.52, 13.83) * mm, "end": v(-10.57, 13.84) * mm});
            skLineSegment(sketch, "E370", {"start": v(-13.27, -14.98) * mm, "end": v(-13.36, -14.97) * mm});
            skLineSegment(sketch, "E371", {"start": v(13.36, 14.97) * mm, "end": v(13.27, 14.98) * mm});
            skLineSegment(sketch, "E372", {"start": v(-12.98, -13.84) * mm, "end": v(-13.03, -13.83) * mm});
            skLineSegment(sketch, "E373", {"start": v(13.03, -9.72) * mm, "end": v(12.98, -9.7) * mm});
            skLineSegment(sketch, "E374", {"start": v(-12.98, 9.7) * mm, "end": v(-13.03, 9.72) * mm});
            skLineSegment(sketch, "E375", {"start": v(13.03, 13.83) * mm, "end": v(12.98, 13.84) * mm});
            skLineSegment(sketch, "E376", {"start": v(-0.44, -3.62) * mm, "end": v(-0.61, -3.6) * mm});
            skLineSegment(sketch, "E377", {"start": v(0.61, 3.6) * mm, "end": v(0.44, 3.62) * mm});
            skLineSegment(sketch, "E378", {"start": v(12.98, -9.7) * mm, "end": v(12.94, -9.7) * mm});
            skLineSegment(sketch, "E379", {"start": v(-12.94, 9.7) * mm, "end": v(-12.98, 9.7) * mm});
            skLineSegment(sketch, "E380", {"start": v(-10.57, -9.7) * mm, "end": v(-10.61, -9.7) * mm});
            skLineSegment(sketch, "E381", {"start": v(10.61, 9.7) * mm, "end": v(10.57, 9.7) * mm});
            skLineSegment(sketch, "E382", {"start": v(-13.18, -15) * mm, "end": v(-13.27, -14.98) * mm});
            skLineSegment(sketch, "E383", {"start": v(13.27, 14.98) * mm, "end": v(13.18, 15) * mm});
            skLineSegment(sketch, "E384", {"start": v(-12.94, -13.85) * mm, "end": v(-12.98, -13.84) * mm});
            skLineSegment(sketch, "E385", {"start": v(12.98, 13.84) * mm, "end": v(12.94, 13.85) * mm});
            skLineSegment(sketch, "E386", {"start": v(10.61, -13.85) * mm, "end": v(10.57, -13.84) * mm});
            skLineSegment(sketch, "E387", {"start": v(-10.57, 13.84) * mm, "end": v(-10.61, 13.85) * mm});
            skLineSegment(sketch, "E388", {"start": v(-0.26, -3.64) * mm, "end": v(-0.44, -3.62) * mm});
            skLineSegment(sketch, "E389", {"start": v(0.44, 3.62) * mm, "end": v(0.26, 3.64) * mm});
            skLineSegment(sketch, "E390", {"start": v(-13.09, -15) * mm, "end": v(-13.18, -15) * mm});
            skLineSegment(sketch, "E391", {"start": v(10.66, -13.85) * mm, "end": v(10.61, -13.85) * mm});
            skLineSegment(sketch, "E392", {"start": v(-12.9, -13.85) * mm, "end": v(-12.94, -13.85) * mm});
            skLineSegment(sketch, "E393", {"start": v(12.94, 13.85) * mm, "end": v(12.9, 13.85) * mm});
            skLineSegment(sketch, "E394", {"start": v(-10.61, 13.85) * mm, "end": v(-10.66, 13.85) * mm});
            skLineSegment(sketch, "E395", {"start": v(13.18, 15) * mm, "end": v(13.09, 15) * mm});
            skLineSegment(sketch, "E396", {"start": v(12.94, -9.7) * mm, "end": v(12.9, -9.7) * mm});
            skLineSegment(sketch, "E397", {"start": v(-10.61, -9.7) * mm, "end": v(-10.66, -9.7) * mm});
            skLineSegment(sketch, "E398", {"start": v(10.66, 9.7) * mm, "end": v(10.61, 9.7) * mm});
            skLineSegment(sketch, "E399", {"start": v(-12.9, 9.7) * mm, "end": v(-12.94, 9.7) * mm});
            skLineSegment(sketch, "E400", {"start": v(-0.09, -3.65) * mm, "end": v(-0.26, -3.64) * mm});
            skLineSegment(sketch, "E401", {"start": v(0.26, 3.64) * mm, "end": v(0.09, 3.65) * mm});
            skLineSegment(sketch, "E402", {"start": v(-13, -15) * mm, "end": v(-13.09, -15) * mm});
            skLineSegment(sketch, "E403", {"start": v(10.7, -13.85) * mm, "end": v(10.66, -13.85) * mm});
            skLineSegment(sketch, "E404", {"start": v(-12.85, -13.85) * mm, "end": v(-12.9, -13.85) * mm});
            skLineSegment(sketch, "E405", {"start": v(12.9, -9.7) * mm, "end": v(12.85, -9.7) * mm});
            skLineSegment(sketch, "E406", {"start": v(-10.66, -9.7) * mm, "end": v(-10.7, -9.7) * mm});
            skLineSegment(sketch, "E407", {"start": v(10.7, 9.7) * mm, "end": v(10.66, 9.7) * mm});
            skLineSegment(sketch, "E408", {"start": v(-12.85, 9.7) * mm, "end": v(-12.9, 9.7) * mm});
            skLineSegment(sketch, "E409", {"start": v(12.9, 13.85) * mm, "end": v(12.85, 13.85) * mm});
            skLineSegment(sketch, "E410", {"start": v(-10.66, 13.85) * mm, "end": v(-10.7, 13.85) * mm});
            skLineSegment(sketch, "E411", {"start": v(13.09, 15) * mm, "end": v(13, 15) * mm});
            skLineSegment(sketch, "E412", {"start": v(8.25, -12.8) * mm, "end": v(-8.25, -12.8) * mm});
            skLineSegment(sketch, "E413", {"start": v(-4, 12.8) * mm, "end": v(-8.25, 12.8) * mm});
            skLineSegment(sketch, "E414", {"start": v(-13, -15) * mm, "end": v(13, -15) * mm});
            skLineSegment(sketch, "E415", {"start": v(10.7, -13.85) * mm, "end": v(12.85, -13.85) * mm});
            skLineSegment(sketch, "E416", {"start": v(-12.85, -13.85) * mm, "end": v(-10.7, -13.85) * mm});
            skLineSegment(sketch, "E417", {"start": v(10.7, -9.7) * mm, "end": v(12.85, -9.7) * mm});
            skLineSegment(sketch, "E418", {"start": v(-12.85, -9.7) * mm, "end": v(-10.7, -9.7) * mm});
            skLineSegment(sketch, "E419", {"start": v(10.05, -8.25) * mm, "end": v(12.8, -8.25) * mm});
            skLineSegment(sketch, "E420", {"start": v(-12.8, -8.25) * mm, "end": v(-10.05, -8.25) * mm});
            skLineSegment(sketch, "E421", {"start": v(0.92, -6) * mm, "end": v(4.2, -6) * mm});
            skLineSegment(sketch, "E422", {"start": v(-4.2, -6) * mm, "end": v(-0.92, -6) * mm});
            skLineSegment(sketch, "E423", {"start": v(-0.09, -3.65) * mm, "end": v(0.09, -3.65) * mm});
            skLineSegment(sketch, "E424", {"start": v(-0.09, 3.65) * mm, "end": v(0.09, 3.65) * mm});
            skLineSegment(sketch, "E425", {"start": v(0.92, 6) * mm, "end": v(4.2, 6) * mm});
            skLineSegment(sketch, "E426", {"start": v(-4.2, 6) * mm, "end": v(-0.92, 6) * mm});
            skLineSegment(sketch, "E427", {"start": v(10.05, 8.25) * mm, "end": v(12.8, 8.25) * mm});
            skLineSegment(sketch, "E428", {"start": v(-12.8, 8.25) * mm, "end": v(-10.05, 8.25) * mm});
            skLineSegment(sketch, "E429", {"start": v(10.7, 9.7) * mm, "end": v(12.85, 9.7) * mm});
            skLineSegment(sketch, "E430", {"start": v(-12.85, 9.7) * mm, "end": v(-10.7, 9.7) * mm});
            skLineSegment(sketch, "E431", {"start": v(10.7, 13.85) * mm, "end": v(12.85, 13.85) * mm});
            skLineSegment(sketch, "E432", {"start": v(-12.85, 13.85) * mm, "end": v(-10.7, 13.85) * mm});
            skLineSegment(sketch, "E433", {"start": v(-4.5, 14.5) * mm, "end": v(-4, 14.5) * mm});
            skLineSegment(sketch, "E434", {"start": v(4, 14.5) * mm, "end": v(4.5, 14.5) * mm});
            skLineSegment(sketch, "E435", {"start": v(-13, 15) * mm, "end": v(-4.5, 15) * mm});
            skLineSegment(sketch, "E436", {"start": v(4.5, 15) * mm, "end": v(13, 15) * mm});
            skLineSegment(sketch, "E437", {"start": v(4, 12.8) * mm, "end": v(8.25, 12.8) * mm});
            skLineSegment(sketch, "E438", {"start": v(13, -15) * mm, "end": v(13.09, -15) * mm});
            skLineSegment(sketch, "E439", {"start": v(12.85, -13.85) * mm, "end": v(12.9, -13.85) * mm});
            skLineSegment(sketch, "E440", {"start": v(-10.7, -13.85) * mm, "end": v(-10.66, -13.85) * mm});
            skLineSegment(sketch, "E441", {"start": v(10.66, -9.7) * mm, "end": v(10.7, -9.7) * mm});
            skLineSegment(sketch, "E442", {"start": v(-12.9, -9.7) * mm, "end": v(-12.85, -9.7) * mm});
            skLineSegment(sketch, "E443", {"start": v(12.85, 9.7) * mm, "end": v(12.9, 9.7) * mm});
            skLineSegment(sketch, "E444", {"start": v(-10.7, 9.7) * mm, "end": v(-10.66, 9.7) * mm});
            skLineSegment(sketch, "E445", {"start": v(10.66, 13.85) * mm, "end": v(10.7, 13.85) * mm});
            skLineSegment(sketch, "E446", {"start": v(-12.9, 13.85) * mm, "end": v(-12.85, 13.85) * mm});
            skLineSegment(sketch, "E447", {"start": v(-13.09, 15) * mm, "end": v(-13, 15) * mm});
            skLineSegment(sketch, "E448", {"start": v(0.09, -3.65) * mm, "end": v(0.26, -3.64) * mm});
            skLineSegment(sketch, "E449", {"start": v(-0.26, 3.64) * mm, "end": v(-0.09, 3.65) * mm});
            skLineSegment(sketch, "E450", {"start": v(10.61, -9.7) * mm, "end": v(10.66, -9.7) * mm});
            skLineSegment(sketch, "E451", {"start": v(-12.94, -9.7) * mm, "end": v(-12.9, -9.7) * mm});
            skLineSegment(sketch, "E452", {"start": v(12.9, 9.7) * mm, "end": v(12.94, 9.7) * mm});
            skLineSegment(sketch, "E453", {"start": v(-10.66, 9.7) * mm, "end": v(-10.61, 9.7) * mm});
            skLineSegment(sketch, "E454", {"start": v(13.09, -15) * mm, "end": v(13.18, -15) * mm});
            skLineSegment(sketch, "E455", {"start": v(12.9, -13.85) * mm, "end": v(12.94, -13.85) * mm});
            skLineSegment(sketch, "E456", {"start": v(-10.66, -13.85) * mm, "end": v(-10.61, -13.85) * mm});
            skLineSegment(sketch, "E457", {"start": v(10.61, 13.85) * mm, "end": v(10.66, 13.85) * mm});
            skLineSegment(sketch, "E458", {"start": v(-12.94, 13.85) * mm, "end": v(-12.9, 13.85) * mm});
            skLineSegment(sketch, "E459", {"start": v(-13.18, 15) * mm, "end": v(-13.09, 15) * mm});
            skLineSegment(sketch, "E460", {"start": v(0.26, -3.64) * mm, "end": v(0.44, -3.62) * mm});
            skLineSegment(sketch, "E461", {"start": v(-0.44, 3.62) * mm, "end": v(-0.26, 3.64) * mm});
            skLineSegment(sketch, "E462", {"start": v(-10.61, -13.85) * mm, "end": v(-10.57, -13.84) * mm});
            skLineSegment(sketch, "E463", {"start": v(10.57, 13.84) * mm, "end": v(10.61, 13.85) * mm});
            skLineSegment(sketch, "E464", {"start": v(12.94, -13.85) * mm, "end": v(12.98, -13.84) * mm});
            skLineSegment(sketch, "E465", {"start": v(-12.98, 13.84) * mm, "end": v(-12.94, 13.85) * mm});
            skLineSegment(sketch, "E466", {"start": v(13.18, -15) * mm, "end": v(13.27, -14.98) * mm});
            skLineSegment(sketch, "E467", {"start": v(-13.27, 14.98) * mm, "end": v(-13.18, 15) * mm});
            skLineSegment(sketch, "E468", {"start": v(10.57, -9.7) * mm, "end": v(10.61, -9.7) * mm});
            skLineSegment(sketch, "E469", {"start": v(-10.61, 9.7) * mm, "end": v(-10.57, 9.7) * mm});
            skLineSegment(sketch, "E470", {"start": v(-12.98, -9.7) * mm, "end": v(-12.94, -9.7) * mm});
            skLineSegment(sketch, "E471", {"start": v(12.94, 9.7) * mm, "end": v(12.98, 9.7) * mm});
            skLineSegment(sketch, "E472", {"start": v(0.44, -3.62) * mm, "end": v(0.61, -3.6) * mm});
            skLineSegment(sketch, "E473", {"start": v(-0.61, 3.6) * mm, "end": v(-0.44, 3.62) * mm});
            skLineSegment(sketch, "E474", {"start": v(12.98, -13.84) * mm, "end": v(13.03, -13.83) * mm});
            skLineSegment(sketch, "E475", {"start": v(-13.03, -9.72) * mm, "end": v(-12.98, -9.7) * mm});
            skLineSegment(sketch, "E476", {"start": v(12.98, 9.7) * mm, "end": v(13.03, 9.72) * mm});
            skLineSegment(sketch, "E477", {"start": v(-13.03, 13.83) * mm, "end": v(-12.98, 13.84) * mm});
            skLineSegment(sketch, "E478", {"start": v(13.27, -14.98) * mm, "end": v(13.36, -14.97) * mm});
            skLineSegment(sketch, "E479", {"start": v(-13.36, 14.97) * mm, "end": v(-13.27, 14.98) * mm});
            skLineSegment(sketch, "E480", {"start": v(-10.57, -13.84) * mm, "end": v(-10.52, -13.83) * mm});
            skLineSegment(sketch, "E481", {"start": v(10.52, -9.72) * mm, "end": v(10.57, -9.7) * mm});
            skLineSegment(sketch, "E482", {"start": v(-10.57, 9.7) * mm, "end": v(-10.52, 9.72) * mm});
            skLineSegment(sketch, "E483", {"start": v(10.52, 13.83) * mm, "end": v(10.57, 13.84) * mm});
            skLineSegment(sketch, "E484", {"start": v(0.61, -3.6) * mm, "end": v(0.79, -3.56) * mm});
            skLineSegment(sketch, "E485", {"start": v(-0.79, 3.56) * mm, "end": v(-0.61, 3.6) * mm});
            skLineSegment(sketch, "E486", {"start": v(13.36, -14.97) * mm, "end": v(13.45, -14.95) * mm});
            skLineSegment(sketch, "E487", {"start": v(-13.45, 14.95) * mm, "end": v(-13.36, 14.97) * mm});
            skLineSegment(sketch, "E488", {"start": v(13.03, -13.83) * mm, "end": v(13.07, -13.82) * mm});
            skLineSegment(sketch, "E489", {"start": v(-10.52, -13.83) * mm, "end": v(-10.48, -13.82) * mm});
            skLineSegment(sketch, "E490", {"start": v(10.48, -9.73) * mm, "end": v(10.52, -9.72) * mm});
            skLineSegment(sketch, "E491", {"start": v(-13.07, -9.73) * mm, "end": v(-13.03, -9.72) * mm});
            skLineSegment(sketch, "E492", {"start": v(13.03, 9.72) * mm, "end": v(13.07, 9.73) * mm});
            skLineSegment(sketch, "E493", {"start": v(-10.52, 9.72) * mm, "end": v(-10.48, 9.73) * mm});
            skLineSegment(sketch, "E494", {"start": v(10.48, 13.82) * mm, "end": v(10.52, 13.83) * mm});
            skLineSegment(sketch, "E495", {"start": v(-13.07, 13.82) * mm, "end": v(-13.03, 13.83) * mm});
            skLineSegment(sketch, "E496", {"start": v(0.79, -3.56) * mm, "end": v(0.96, -3.52) * mm});
            skLineSegment(sketch, "E497", {"start": v(-0.96, 3.52) * mm, "end": v(-0.79, 3.56) * mm});
            skLineSegment(sketch, "E498", {"start": v(13.45, -14.95) * mm, "end": v(13.53, -14.93) * mm});
            skLineSegment(sketch, "E499", {"start": v(-10.48, -13.82) * mm, "end": v(-10.43, -13.81) * mm});
            skLineSegment(sketch, "E500", {"start": v(10.43, -9.74) * mm, "end": v(10.48, -9.73) * mm});
            skLineSegment(sketch, "E501", {"start": v(-10.48, 9.73) * mm, "end": v(-10.43, 9.74) * mm});
            skLineSegment(sketch, "E502", {"start": v(10.43, 13.81) * mm, "end": v(10.48, 13.82) * mm});
            skLineSegment(sketch, "E503", {"start": v(-13.53, 14.93) * mm, "end": v(-13.45, 14.95) * mm});
            skLineSegment(sketch, "E504", {"start": v(13.07, -13.82) * mm, "end": v(13.12, -13.81) * mm});
            skLineSegment(sketch, "E505", {"start": v(-13.12, -9.74) * mm, "end": v(-13.07, -9.73) * mm});
            skLineSegment(sketch, "E506", {"start": v(13.07, 9.73) * mm, "end": v(13.12, 9.74) * mm});
            skLineSegment(sketch, "E507", {"start": v(-13.12, 13.81) * mm, "end": v(-13.07, 13.82) * mm});
            skLineSegment(sketch, "E508", {"start": v(0.96, -3.52) * mm, "end": v(1.13, -3.47) * mm});
            skLineSegment(sketch, "E509", {"start": v(-1.13, 3.47) * mm, "end": v(-0.96, 3.52) * mm});
            skLineSegment(sketch, "E510", {"start": v(13.12, -13.81) * mm, "end": v(13.16, -13.8) * mm});
            skLineSegment(sketch, "E511", {"start": v(-13.16, -9.75) * mm, "end": v(-13.12, -9.74) * mm});
            skLineSegment(sketch, "E512", {"start": v(13.12, 9.74) * mm, "end": v(13.16, 9.75) * mm});
            skLineSegment(sketch, "E513", {"start": v(-13.16, 13.8) * mm, "end": v(-13.12, 13.81) * mm});
            skLineSegment(sketch, "E514", {"start": v(-10.43, -13.81) * mm, "end": v(-10.4, -13.8) * mm});
            skLineSegment(sketch, "E515", {"start": v(10.4, -9.75) * mm, "end": v(10.43, -9.74) * mm});
            skLineSegment(sketch, "E516", {"start": v(-10.43, 9.74) * mm, "end": v(-10.4, 9.75) * mm});
            skLineSegment(sketch, "E517", {"start": v(10.4, 13.8) * mm, "end": v(10.43, 13.81) * mm});
            skLineSegment(sketch, "E518", {"start": v(13.53, -14.93) * mm, "end": v(13.62, -14.9) * mm});
            skLineSegment(sketch, "E519", {"start": v(-13.62, 14.9) * mm, "end": v(-13.53, 14.93) * mm});
            skLineSegment(sketch, "E520", {"start": v(13.62, -14.9) * mm, "end": v(13.7, -14.87) * mm});
            skLineSegment(sketch, "E521", {"start": v(-13.7, 14.87) * mm, "end": v(-13.62, 14.9) * mm});
            skLineSegment(sketch, "E522", {"start": v(13.16, -13.8) * mm, "end": v(13.2, -13.79) * mm});
            skLineSegment(sketch, "E523", {"start": v(-10.4, -13.8) * mm, "end": v(-10.35, -13.79) * mm});
            skLineSegment(sketch, "E524", {"start": v(10.35, -9.76) * mm, "end": v(10.4, -9.75) * mm});
            skLineSegment(sketch, "E525", {"start": v(-13.2, -9.76) * mm, "end": v(-13.16, -9.75) * mm});
            skLineSegment(sketch, "E526", {"start": v(13.16, 9.75) * mm, "end": v(13.2, 9.76) * mm});
            skLineSegment(sketch, "E527", {"start": v(-10.4, 9.75) * mm, "end": v(-10.35, 9.76) * mm});
            skLineSegment(sketch, "E528", {"start": v(10.35, 13.79) * mm, "end": v(10.4, 13.8) * mm});
            skLineSegment(sketch, "E529", {"start": v(-13.2, 13.79) * mm, "end": v(-13.16, 13.8) * mm});
            skLineSegment(sketch, "E530", {"start": v(1.13, -3.47) * mm, "end": v(1.3, -3.41) * mm});
            skLineSegment(sketch, "E531", {"start": v(-1.3, 3.41) * mm, "end": v(-1.13, 3.47) * mm});
            skLineSegment(sketch, "E532", {"start": v(13.7, -14.87) * mm, "end": v(13.79, -14.84) * mm});
            skLineSegment(sketch, "E533", {"start": v(-13.79, 14.84) * mm, "end": v(-13.7, 14.87) * mm});
            skLineSegment(sketch, "E534", {"start": v(10.3, -9.78) * mm, "end": v(10.35, -9.76) * mm});
            skLineSegment(sketch, "E535", {"start": v(-13.24, -9.78) * mm, "end": v(-13.2, -9.76) * mm});
            skLineSegment(sketch, "E536", {"start": v(13.2, 9.76) * mm, "end": v(13.24, 9.78) * mm});
            skLineSegment(sketch, "E537", {"start": v(-10.35, 9.76) * mm, "end": v(-10.3, 9.78) * mm});
            skLineSegment(sketch, "E538", {"start": v(13.2, -13.79) * mm, "end": v(13.24, -13.77) * mm});
            skLineSegment(sketch, "E539", {"start": v(-10.35, -13.79) * mm, "end": v(-10.3, -13.77) * mm});
            skLineSegment(sketch, "E540", {"start": v(10.3, 13.77) * mm, "end": v(10.35, 13.79) * mm});
            skLineSegment(sketch, "E541", {"start": v(-13.24, 13.77) * mm, "end": v(-13.2, 13.79) * mm});
            skLineSegment(sketch, "E542", {"start": v(1.3, -3.41) * mm, "end": v(1.46, -3.35) * mm});
            skLineSegment(sketch, "E543", {"start": v(-1.46, 3.35) * mm, "end": v(-1.3, 3.41) * mm});
            skLineSegment(sketch, "E544", {"start": v(13.24, -13.77) * mm, "end": v(13.28, -13.75) * mm});
            skLineSegment(sketch, "E545", {"start": v(-10.3, -13.77) * mm, "end": v(-10.27, -13.75) * mm});
            skLineSegment(sketch, "E546", {"start": v(10.27, 13.75) * mm, "end": v(10.3, 13.77) * mm});
            skLineSegment(sketch, "E547", {"start": v(-13.28, 13.75) * mm, "end": v(-13.24, 13.77) * mm});
            skLineSegment(sketch, "E548", {"start": v(10.27, -9.8) * mm, "end": v(10.3, -9.78) * mm});
            skLineSegment(sketch, "E549", {"start": v(-13.28, -9.8) * mm, "end": v(-13.24, -9.78) * mm});
            skLineSegment(sketch, "E550", {"start": v(13.24, 9.78) * mm, "end": v(13.28, 9.8) * mm});
            skLineSegment(sketch, "E551", {"start": v(-10.3, 9.78) * mm, "end": v(-10.27, 9.8) * mm});
            skLineSegment(sketch, "E552", {"start": v(13.79, -14.84) * mm, "end": v(13.87, -14.8) * mm});
            skLineSegment(sketch, "E553", {"start": v(-13.87, 14.8) * mm, "end": v(-13.79, 14.84) * mm});
            skLineSegment(sketch, "E554", {"start": v(1.46, -3.35) * mm, "end": v(1.62, -3.27) * mm});
            skLineSegment(sketch, "E555", {"start": v(-1.62, 3.27) * mm, "end": v(-1.46, 3.35) * mm});
            skLineSegment(sketch, "E556", {"start": v(13.28, -13.75) * mm, "end": v(13.32, -13.73) * mm});
            skLineSegment(sketch, "E557", {"start": v(-10.27, -13.75) * mm, "end": v(-10.23, -13.73) * mm});
            skLineSegment(sketch, "E558", {"start": v(10.23, 13.73) * mm, "end": v(10.27, 13.75) * mm});
            skLineSegment(sketch, "E559", {"start": v(-13.32, 13.73) * mm, "end": v(-13.28, 13.75) * mm});
            skLineSegment(sketch, "E560", {"start": v(13.87, -14.8) * mm, "end": v(13.95, -14.76) * mm});
            skLineSegment(sketch, "E561", {"start": v(-13.95, 14.76) * mm, "end": v(-13.87, 14.8) * mm});
            skLineSegment(sketch, "E562", {"start": v(10.23, -9.82) * mm, "end": v(10.27, -9.8) * mm});
            skLineSegment(sketch, "E563", {"start": v(-13.32, -9.82) * mm, "end": v(-13.28, -9.8) * mm});
            skLineSegment(sketch, "E564", {"start": v(13.28, 9.8) * mm, "end": v(13.32, 9.82) * mm});
            skLineSegment(sketch, "E565", {"start": v(-10.27, 9.8) * mm, "end": v(-10.23, 9.82) * mm});
            skLineSegment(sketch, "E566", {"start": v(10.19, -9.84) * mm, "end": v(10.23, -9.82) * mm});
            skLineSegment(sketch, "E567", {"start": v(-10.23, 9.82) * mm, "end": v(-10.19, 9.84) * mm});
            skLineSegment(sketch, "E568", {"start": v(-13.36, -9.84) * mm, "end": v(-13.32, -9.82) * mm});
            skLineSegment(sketch, "E569", {"start": v(13.32, 9.82) * mm, "end": v(13.36, 9.84) * mm});
            skLineSegment(sketch, "E570", {"start": v(13.95, -14.76) * mm, "end": v(14.03, -14.72) * mm});
            skLineSegment(sketch, "E571", {"start": v(-14.03, 14.72) * mm, "end": v(-13.95, 14.76) * mm});
            skLineSegment(sketch, "E572", {"start": v(-10.23, -13.73) * mm, "end": v(-10.19, -13.7) * mm});
            skLineSegment(sketch, "E573", {"start": v(10.19, 13.7) * mm, "end": v(10.23, 13.73) * mm});
            skLineSegment(sketch, "E574", {"start": v(13.32, -13.73) * mm, "end": v(13.36, -13.7) * mm});
            skLineSegment(sketch, "E575", {"start": v(-13.36, 13.7) * mm, "end": v(-13.32, 13.73) * mm});
            skLineSegment(sketch, "E576", {"start": v(-0.92, -6) * mm, "end": v(0, -5.47) * mm});
            skLineSegment(sketch, "E577", {"start": v(0, 5.47) * mm, "end": v(0.92, 6) * mm});
            skLineSegment(sketch, "E578", {"start": v(13.36, -13.7) * mm, "end": v(13.4, -13.68) * mm});
            skLineSegment(sketch, "E579", {"start": v(-13.4, 13.68) * mm, "end": v(-13.36, 13.7) * mm});
            skLineSegment(sketch, "E580", {"start": v(-10.19, -13.7) * mm, "end": v(-10.15, -13.68) * mm});
            skLineSegment(sketch, "E581", {"start": v(10.15, 13.68) * mm, "end": v(10.19, 13.7) * mm});
            skLineSegment(sketch, "E582", {"start": v(14.03, -14.72) * mm, "end": v(14.1, -14.67) * mm});
            skLineSegment(sketch, "E583", {"start": v(-14.1, 14.67) * mm, "end": v(-14.03, 14.72) * mm});
            skLineSegment(sketch, "E584", {"start": v(-13.4, -9.87) * mm, "end": v(-13.36, -9.84) * mm});
            skLineSegment(sketch, "E585", {"start": v(13.36, 9.84) * mm, "end": v(13.4, 9.87) * mm});
            skLineSegment(sketch, "E586", {"start": v(10.15, -9.87) * mm, "end": v(10.19, -9.84) * mm});
            skLineSegment(sketch, "E587", {"start": v(-10.19, 9.84) * mm, "end": v(-10.15, 9.87) * mm});
            skLineSegment(sketch, "E588", {"start": v(13.4, -13.68) * mm, "end": v(13.44, -13.66) * mm});
            skLineSegment(sketch, "E589", {"start": v(-10.15, -13.68) * mm, "end": v(-10.11, -13.66) * mm});
            skLineSegment(sketch, "E590", {"start": v(10.11, -9.9) * mm, "end": v(10.15, -9.87) * mm});
            skLineSegment(sketch, "E591", {"start": v(-13.44, -9.9) * mm, "end": v(-13.4, -9.87) * mm});
            skLineSegment(sketch, "E592", {"start": v(13.4, 9.87) * mm, "end": v(13.44, 9.9) * mm});
            skLineSegment(sketch, "E593", {"start": v(-10.15, 9.87) * mm, "end": v(-10.11, 9.9) * mm});
            skLineSegment(sketch, "E594", {"start": v(10.11, 13.66) * mm, "end": v(10.15, 13.68) * mm});
            skLineSegment(sketch, "E595", {"start": v(-13.44, 13.66) * mm, "end": v(-13.4, 13.68) * mm});
            skLineSegment(sketch, "E596", {"start": v(14.1, -14.67) * mm, "end": v(14.18, -14.62) * mm});
            skLineSegment(sketch, "E597", {"start": v(-14.18, 14.62) * mm, "end": v(-14.1, 14.67) * mm});
            skLineSegment(sketch, "E598", {"start": v(3.12, -4.53) * mm, "end": v(3.35, -4.36) * mm});
            skLineSegment(sketch, "E599", {"start": v(-3.35, 4.36) * mm, "end": v(-3.12, 4.53) * mm});
            skLineSegment(sketch, "E600", {"start": v(10.08, -9.92) * mm, "end": v(10.11, -9.9) * mm});
            skLineSegment(sketch, "E601", {"start": v(-13.47, -9.92) * mm, "end": v(-13.44, -9.9) * mm});
            skLineSegment(sketch, "E602", {"start": v(13.44, 9.9) * mm, "end": v(13.47, 9.92) * mm});
            skLineSegment(sketch, "E603", {"start": v(-10.11, 9.9) * mm, "end": v(-10.08, 9.92) * mm});
            skLineSegment(sketch, "E604", {"start": v(14.18, -14.62) * mm, "end": v(14.25, -14.56) * mm});
            skLineSegment(sketch, "E605", {"start": v(-14.25, 14.56) * mm, "end": v(-14.18, 14.62) * mm});
            skLineSegment(sketch, "E606", {"start": v(13.44, -13.66) * mm, "end": v(13.47, -13.63) * mm});
            skLineSegment(sketch, "E607", {"start": v(-10.11, -13.66) * mm, "end": v(-10.08, -13.63) * mm});
            skLineSegment(sketch, "E608", {"start": v(10.08, 13.63) * mm, "end": v(10.11, 13.66) * mm});
            skLineSegment(sketch, "E609", {"start": v(-13.47, 13.63) * mm, "end": v(-13.44, 13.66) * mm});
            skLineSegment(sketch, "E610", {"start": v(3.35, -4.36) * mm, "end": v(3.57, -4.18) * mm});
            skLineSegment(sketch, "E611", {"start": v(-3.57, 4.18) * mm, "end": v(-3.35, 4.36) * mm});
            skLineSegment(sketch, "E612", {"start": v(14.25, -14.56) * mm, "end": v(14.32, -14.5) * mm});
            skLineSegment(sketch, "E613", {"start": v(-10.08, -13.63) * mm, "end": v(-10.04, -13.6) * mm});
            skLineSegment(sketch, "E614", {"start": v(10.04, 13.6) * mm, "end": v(10.08, 13.63) * mm});
            skLineSegment(sketch, "E615", {"start": v(-14.32, 14.5) * mm, "end": v(-14.25, 14.56) * mm});
            skLineSegment(sketch, "E616", {"start": v(13.47, -13.63) * mm, "end": v(13.5, -13.6) * mm});
            skLineSegment(sketch, "E617", {"start": v(-13.5, 13.6) * mm, "end": v(-13.47, 13.63) * mm});
            skLineSegment(sketch, "E618", {"start": v(10.04, -9.95) * mm, "end": v(10.08, -9.92) * mm});
            skLineSegment(sketch, "E619", {"start": v(-10.08, 9.92) * mm, "end": v(-10.04, 9.95) * mm});
            skLineSegment(sketch, "E620", {"start": v(-13.5, -9.95) * mm, "end": v(-13.47, -9.92) * mm});
            skLineSegment(sketch, "E621", {"start": v(13.47, 9.92) * mm, "end": v(13.5, 9.95) * mm});
            skLineSegment(sketch, "E622", {"start": v(-3.12, -4.53) * mm, "end": v(-1.62, -3.27) * mm});
            skLineSegment(sketch, "E623", {"start": v(1.62, 3.27) * mm, "end": v(3.12, 4.53) * mm});
            skLineSegment(sketch, "E624", {"start": v(3.57, -4.18) * mm, "end": v(3.79, -3.99) * mm});
            skLineSegment(sketch, "E625", {"start": v(-3.79, 3.99) * mm, "end": v(-3.57, 4.18) * mm});
            skLineSegment(sketch, "E626", {"start": v(13.5, -13.6) * mm, "end": v(13.54, -13.57) * mm});
            skLineSegment(sketch, "E627", {"start": v(-10.04, -13.6) * mm, "end": v(-10, -13.57) * mm});
            skLineSegment(sketch, "E628", {"start": v(10, -9.98) * mm, "end": v(10.04, -9.95) * mm});
            skLineSegment(sketch, "E629", {"start": v(-13.54, -9.98) * mm, "end": v(-13.5, -9.95) * mm});
            skLineSegment(sketch, "E630", {"start": v(13.5, 9.95) * mm, "end": v(13.54, 9.98) * mm});
            skLineSegment(sketch, "E631", {"start": v(-10.04, 9.95) * mm, "end": v(-10, 9.98) * mm});
            skLineSegment(sketch, "E632", {"start": v(10, 13.57) * mm, "end": v(10.04, 13.6) * mm});
            skLineSegment(sketch, "E633", {"start": v(-13.54, 13.57) * mm, "end": v(-13.5, 13.6) * mm});
            skLineSegment(sketch, "E634", {"start": v(14.32, -14.5) * mm, "end": v(14.38, -14.45) * mm});
            skLineSegment(sketch, "E635", {"start": v(-14.38, 14.45) * mm, "end": v(-14.32, 14.5) * mm});
            skLineSegment(sketch, "E636", {"start": v(-13.57, -10) * mm, "end": v(-13.54, -9.98) * mm});
            skLineSegment(sketch, "E637", {"start": v(13.54, 9.98) * mm, "end": v(13.57, 10) * mm});
            skLineSegment(sketch, "E638", {"start": v(14.38, -14.45) * mm, "end": v(14.45, -14.38) * mm});
            skLineSegment(sketch, "E639", {"start": v(13.54, -13.57) * mm, "end": v(13.57, -13.54) * mm});
            skLineSegment(sketch, "E640", {"start": v(9.98, -10) * mm, "end": v(10, -9.98) * mm});
            skLineSegment(sketch, "E641", {"start": v(-10.05, -8.25) * mm, "end": v(-6, -4.2) * mm});
            skLineSegment(sketch, "E642", {"start": v(3.79, -3.99) * mm, "end": v(3.99, -3.79) * mm});
            skLineSegment(sketch, "E643", {"start": v(-3.99, 3.79) * mm, "end": v(-3.79, 3.99) * mm});
            skLineSegment(sketch, "E644", {"start": v(6, 4.2) * mm, "end": v(10.05, 8.25) * mm});
            skLineSegment(sketch, "E645", {"start": v(-8.25, -10.05) * mm, "end": v(-4.2, -6) * mm});
            skLineSegment(sketch, "E646", {"start": v(4.2, 6) * mm, "end": v(8.25, 10.05) * mm});
            skLineSegment(sketch, "E647", {"start": v(-10, 9.98) * mm, "end": v(-9.98, 10) * mm});
            skLineSegment(sketch, "E648", {"start": v(-13.57, 13.54) * mm, "end": v(-13.54, 13.57) * mm});
            skLineSegment(sketch, "E649", {"start": v(-14.45, 14.38) * mm, "end": v(-14.38, 14.45) * mm});
            skLineSegment(sketch, "E650", {"start": v(-10, -13.57) * mm, "end": v(-9.98, -13.54) * mm});
            skLineSegment(sketch, "E651", {"start": v(9.98, 13.54) * mm, "end": v(10, 13.57) * mm});
            skLineSegment(sketch, "E652", {"start": v(14.45, -14.38) * mm, "end": v(14.5, -14.32) * mm});
            skLineSegment(sketch, "E653", {"start": v(-14.5, 14.32) * mm, "end": v(-14.45, 14.38) * mm});
            skLineSegment(sketch, "E654", {"start": v(13.57, -13.54) * mm, "end": v(13.6, -13.5) * mm});
            skLineSegment(sketch, "E655", {"start": v(-9.98, -13.54) * mm, "end": v(-9.95, -13.5) * mm});
            skLineSegment(sketch, "E656", {"start": v(9.95, -10.04) * mm, "end": v(9.98, -10) * mm});
            skLineSegment(sketch, "E657", {"start": v(-13.6, -10.04) * mm, "end": v(-13.57, -10) * mm});
            skLineSegment(sketch, "E658", {"start": v(13.57, 10) * mm, "end": v(13.6, 10.04) * mm});
            skLineSegment(sketch, "E659", {"start": v(-9.98, 10) * mm, "end": v(-9.95, 10.04) * mm});
            skLineSegment(sketch, "E660", {"start": v(9.95, 13.5) * mm, "end": v(9.98, 13.54) * mm});
            skLineSegment(sketch, "E661", {"start": v(-13.6, 13.5) * mm, "end": v(-13.57, 13.54) * mm});
            skLineSegment(sketch, "E662", {"start": v(3.99, -3.79) * mm, "end": v(4.18, -3.57) * mm});
            skLineSegment(sketch, "E663", {"start": v(-4.18, 3.57) * mm, "end": v(-3.99, 3.79) * mm});
            skLineSegment(sketch, "E664", {"start": v(-4.53, -3.12) * mm, "end": v(-3.27, -1.62) * mm});
            skLineSegment(sketch, "E665", {"start": v(3.27, 1.62) * mm, "end": v(4.53, 3.12) * mm});
            skLineSegment(sketch, "E666", {"start": v(-9.95, -13.5) * mm, "end": v(-9.92, -13.47) * mm});
            skLineSegment(sketch, "E667", {"start": v(9.92, 13.47) * mm, "end": v(9.95, 13.5) * mm});
            skLineSegment(sketch, "E668", {"start": v(9.92, -10.08) * mm, "end": v(9.95, -10.04) * mm});
            skLineSegment(sketch, "E669", {"start": v(-9.95, 10.04) * mm, "end": v(-9.92, 10.08) * mm});
            skLineSegment(sketch, "E670", {"start": v(13.6, -13.5) * mm, "end": v(13.63, -13.47) * mm});
            skLineSegment(sketch, "E671", {"start": v(-13.63, 13.47) * mm, "end": v(-13.6, 13.5) * mm});
            skLineSegment(sketch, "E672", {"start": v(14.5, -14.32) * mm, "end": v(14.56, -14.25) * mm});
            skLineSegment(sketch, "E673", {"start": v(-13.63, -10.08) * mm, "end": v(-13.6, -10.04) * mm});
            skLineSegment(sketch, "E674", {"start": v(13.6, 10.04) * mm, "end": v(13.63, 10.08) * mm});
            skLineSegment(sketch, "E675", {"start": v(-14.56, 14.25) * mm, "end": v(-14.5, 14.32) * mm});
            skLineSegment(sketch, "E676", {"start": v(4.18, -3.57) * mm, "end": v(4.36, -3.35) * mm});
            skLineSegment(sketch, "E677", {"start": v(-4.36, 3.35) * mm, "end": v(-4.18, 3.57) * mm});
            skLineSegment(sketch, "E678", {"start": v(13.63, -13.47) * mm, "end": v(13.66, -13.44) * mm});
            skLineSegment(sketch, "E679", {"start": v(-13.66, -10.11) * mm, "end": v(-13.63, -10.08) * mm});
            skLineSegment(sketch, "E680", {"start": v(13.63, 10.08) * mm, "end": v(13.66, 10.11) * mm});
            skLineSegment(sketch, "E681", {"start": v(-13.66, 13.44) * mm, "end": v(-13.63, 13.47) * mm});
            skLineSegment(sketch, "E682", {"start": v(14.56, -14.25) * mm, "end": v(14.62, -14.18) * mm});
            skLineSegment(sketch, "E683", {"start": v(-14.62, 14.18) * mm, "end": v(-14.56, 14.25) * mm});
            skLineSegment(sketch, "E684", {"start": v(-9.92, -13.47) * mm, "end": v(-9.9, -13.44) * mm});
            skLineSegment(sketch, "E685", {"start": v(9.9, -10.11) * mm, "end": v(9.92, -10.08) * mm});
            skLineSegment(sketch, "E686", {"start": v(-9.92, 10.08) * mm, "end": v(-9.9, 10.11) * mm});
            skLineSegment(sketch, "E687", {"start": v(9.9, 13.44) * mm, "end": v(9.92, 13.47) * mm});
            skLineSegment(sketch, "E688", {"start": v(4.36, -3.35) * mm, "end": v(4.53, -3.12) * mm});
            skLineSegment(sketch, "E689", {"start": v(-4.53, 3.12) * mm, "end": v(-4.36, 3.35) * mm});
            skLineSegment(sketch, "E690", {"start": v(14.62, -14.18) * mm, "end": v(14.67, -14.1) * mm});
            skLineSegment(sketch, "E691", {"start": v(-14.67, 14.1) * mm, "end": v(-14.62, 14.18) * mm});
            skLineSegment(sketch, "E692", {"start": v(13.66, -13.44) * mm, "end": v(13.68, -13.4) * mm});
            skLineSegment(sketch, "E693", {"start": v(-9.9, -13.44) * mm, "end": v(-9.87, -13.4) * mm});
            skLineSegment(sketch, "E694", {"start": v(9.87, -10.15) * mm, "end": v(9.9, -10.11) * mm});
            skLineSegment(sketch, "E695", {"start": v(-13.68, -10.15) * mm, "end": v(-13.66, -10.11) * mm});
            skLineSegment(sketch, "E696", {"start": v(13.66, 10.11) * mm, "end": v(13.68, 10.15) * mm});
            skLineSegment(sketch, "E697", {"start": v(-9.9, 10.11) * mm, "end": v(-9.87, 10.15) * mm});
            skLineSegment(sketch, "E698", {"start": v(9.87, 13.4) * mm, "end": v(9.9, 13.44) * mm});
            skLineSegment(sketch, "E699", {"start": v(-13.68, 13.4) * mm, "end": v(-13.66, 13.44) * mm});
            skLineSegment(sketch, "E700", {"start": v(9.84, -10.19) * mm, "end": v(9.87, -10.15) * mm});
            skLineSegment(sketch, "E701", {"start": v(-9.87, 10.15) * mm, "end": v(-9.84, 10.19) * mm});
            skLineSegment(sketch, "E702", {"start": v(-9.87, -13.4) * mm, "end": v(-9.84, -13.36) * mm});
            skLineSegment(sketch, "E703", {"start": v(9.84, 13.36) * mm, "end": v(9.87, 13.4) * mm});
            skLineSegment(sketch, "E704", {"start": v(14.67, -14.1) * mm, "end": v(14.72, -14.03) * mm});
            skLineSegment(sketch, "E705", {"start": v(-14.72, 14.03) * mm, "end": v(-14.67, 14.1) * mm});
            skLineSegment(sketch, "E706", {"start": v(-13.7, -10.19) * mm, "end": v(-13.68, -10.15) * mm});
            skLineSegment(sketch, "E707", {"start": v(13.68, 10.15) * mm, "end": v(13.7, 10.19) * mm});
            skLineSegment(sketch, "E708", {"start": v(13.68, -13.4) * mm, "end": v(13.7, -13.36) * mm});
            skLineSegment(sketch, "E709", {"start": v(-13.7, 13.36) * mm, "end": v(-13.68, 13.4) * mm});
            skLineSegment(sketch, "E710", {"start": v(-6, -0.92) * mm, "end": v(-5.47, 0) * mm});
            skLineSegment(sketch, "E711", {"start": v(5.47, 0) * mm, "end": v(6, 0.92) * mm});
            skLineSegment(sketch, "E712", {"start": v(13.7, -13.36) * mm, "end": v(13.73, -13.32) * mm});
            skLineSegment(sketch, "E713", {"start": v(-13.73, 13.32) * mm, "end": v(-13.7, 13.36) * mm});
            skLineSegment(sketch, "E714", {"start": v(-13.73, -10.23) * mm, "end": v(-13.7, -10.19) * mm});
            skLineSegment(sketch, "E715", {"start": v(13.7, 10.19) * mm, "end": v(13.73, 10.23) * mm});
            skLineSegment(sketch, "E716", {"start": v(14.72, -14.03) * mm, "end": v(14.76, -13.95) * mm});
            skLineSegment(sketch, "E717", {"start": v(-14.76, 13.95) * mm, "end": v(-14.72, 14.03) * mm});
            skLineSegment(sketch, "E718", {"start": v(-9.84, -13.36) * mm, "end": v(-9.82, -13.32) * mm});
            skLineSegment(sketch, "E719", {"start": v(9.82, 13.32) * mm, "end": v(9.84, 13.36) * mm});
            skLineSegment(sketch, "E720", {"start": v(9.82, -10.23) * mm, "end": v(9.84, -10.19) * mm});
            skLineSegment(sketch, "E721", {"start": v(-9.84, 10.19) * mm, "end": v(-9.82, 10.23) * mm});
            skLineSegment(sketch, "E722", {"start": v(-9.82, -13.32) * mm, "end": v(-9.8, -13.28) * mm});
            skLineSegment(sketch, "E723", {"start": v(9.8, -10.27) * mm, "end": v(9.82, -10.23) * mm});
            skLineSegment(sketch, "E724", {"start": v(-9.82, 10.23) * mm, "end": v(-9.8, 10.27) * mm});
            skLineSegment(sketch, "E725", {"start": v(9.8, 13.28) * mm, "end": v(9.82, 13.32) * mm});
            skLineSegment(sketch, "E726", {"start": v(14.76, -13.95) * mm, "end": v(14.8, -13.87) * mm});
            skLineSegment(sketch, "E727", {"start": v(-14.8, 13.87) * mm, "end": v(-14.76, 13.95) * mm});
            skLineSegment(sketch, "E728", {"start": v(13.73, -13.32) * mm, "end": v(13.75, -13.28) * mm});
            skLineSegment(sketch, "E729", {"start": v(-13.75, -10.27) * mm, "end": v(-13.73, -10.23) * mm});
            skLineSegment(sketch, "E730", {"start": v(13.73, 10.23) * mm, "end": v(13.75, 10.27) * mm});
            skLineSegment(sketch, "E731", {"start": v(-13.75, 13.28) * mm, "end": v(-13.73, 13.32) * mm});
            skLineSegment(sketch, "E732", {"start": v(3.27, -1.62) * mm, "end": v(3.35, -1.46) * mm});
            skLineSegment(sketch, "E733", {"start": v(-3.35, 1.46) * mm, "end": v(-3.27, 1.62) * mm});
            skLineSegment(sketch, "E734", {"start": v(14.8, -13.87) * mm, "end": v(14.84, -13.79) * mm});
            skLineSegment(sketch, "E735", {"start": v(-14.84, 13.79) * mm, "end": v(-14.8, 13.87) * mm});
            skLineSegment(sketch, "E736", {"start": v(-9.8, -13.28) * mm, "end": v(-9.78, -13.24) * mm});
            skLineSegment(sketch, "E737", {"start": v(9.78, -10.3) * mm, "end": v(9.8, -10.27) * mm});
            skLineSegment(sketch, "E738", {"start": v(-9.8, 10.27) * mm, "end": v(-9.78, 10.3) * mm});
            skLineSegment(sketch, "E739", {"start": v(9.78, 13.24) * mm, "end": v(9.8, 13.28) * mm});
            skLineSegment(sketch, "E740", {"start": v(13.75, -13.28) * mm, "end": v(13.77, -13.24) * mm});
            skLineSegment(sketch, "E741", {"start": v(-13.77, -10.3) * mm, "end": v(-13.75, -10.27) * mm});
            skLineSegment(sketch, "E742", {"start": v(13.75, 10.27) * mm, "end": v(13.77, 10.3) * mm});
            skLineSegment(sketch, "E743", {"start": v(-13.77, 13.24) * mm, "end": v(-13.75, 13.28) * mm});
            skLineSegment(sketch, "E744", {"start": v(3.35, -1.46) * mm, "end": v(3.41, -1.3) * mm});
            skLineSegment(sketch, "E745", {"start": v(-3.41, 1.3) * mm, "end": v(-3.35, 1.46) * mm});
            skLineSegment(sketch, "E746", {"start": v(13.77, -13.24) * mm, "end": v(13.79, -13.2) * mm});
            skLineSegment(sketch, "E747", {"start": v(-13.79, -10.35) * mm, "end": v(-13.77, -10.3) * mm});
            skLineSegment(sketch, "E748", {"start": v(13.77, 10.3) * mm, "end": v(13.79, 10.35) * mm});
            skLineSegment(sketch, "E749", {"start": v(-13.79, 13.2) * mm, "end": v(-13.77, 13.24) * mm});
            skLineSegment(sketch, "E750", {"start": v(-9.78, -13.24) * mm, "end": v(-9.76, -13.2) * mm});
            skLineSegment(sketch, "E751", {"start": v(9.76, -10.35) * mm, "end": v(9.78, -10.3) * mm});
            skLineSegment(sketch, "E752", {"start": v(-9.78, 10.3) * mm, "end": v(-9.76, 10.35) * mm});
            skLineSegment(sketch, "E753", {"start": v(9.76, 13.2) * mm, "end": v(9.78, 13.24) * mm});
            skLineSegment(sketch, "E754", {"start": v(14.84, -13.79) * mm, "end": v(14.87, -13.7) * mm});
            skLineSegment(sketch, "E755", {"start": v(-14.87, 13.7) * mm, "end": v(-14.84, 13.79) * mm});
            skLineSegment(sketch, "E756", {"start": v(3.41, -1.3) * mm, "end": v(3.47, -1.13) * mm});
            skLineSegment(sketch, "E757", {"start": v(-3.47, 1.13) * mm, "end": v(-3.41, 1.3) * mm});
            skLineSegment(sketch, "E758", {"start": v(13.79, -13.2) * mm, "end": v(13.8, -13.16) * mm});
            skLineSegment(sketch, "E759", {"start": v(-9.76, -13.2) * mm, "end": v(-9.75, -13.16) * mm});
            skLineSegment(sketch, "E760", {"start": v(9.75, -10.4) * mm, "end": v(9.76, -10.35) * mm});
            skLineSegment(sketch, "E761", {"start": v(-13.8, -10.4) * mm, "end": v(-13.79, -10.35) * mm});
            skLineSegment(sketch, "E762", {"start": v(13.79, 10.35) * mm, "end": v(13.8, 10.4) * mm});
            skLineSegment(sketch, "E763", {"start": v(-9.76, 10.35) * mm, "end": v(-9.75, 10.4) * mm});
            skLineSegment(sketch, "E764", {"start": v(9.75, 13.16) * mm, "end": v(9.76, 13.2) * mm});
            skLineSegment(sketch, "E765", {"start": v(-13.8, 13.16) * mm, "end": v(-13.79, 13.2) * mm});
            skLineSegment(sketch, "E766", {"start": v(14.87, -13.7) * mm, "end": v(14.9, -13.62) * mm});
            skLineSegment(sketch, "E767", {"start": v(-14.9, 13.62) * mm, "end": v(-14.87, 13.7) * mm});
            skLineSegment(sketch, "E768", {"start": v(14.9, -13.62) * mm, "end": v(14.93, -13.53) * mm});
            skLineSegment(sketch, "E769", {"start": v(-14.93, 13.53) * mm, "end": v(-14.9, 13.62) * mm});
            skLineSegment(sketch, "E770", {"start": v(9.74, -10.43) * mm, "end": v(9.75, -10.4) * mm});
            skLineSegment(sketch, "E771", {"start": v(-13.81, -10.43) * mm, "end": v(-13.8, -10.4) * mm});
            skLineSegment(sketch, "E772", {"start": v(13.8, 10.4) * mm, "end": v(13.81, 10.43) * mm});
            skLineSegment(sketch, "E773", {"start": v(-9.75, 10.4) * mm, "end": v(-9.74, 10.43) * mm});
            skLineSegment(sketch, "E774", {"start": v(13.8, -13.16) * mm, "end": v(13.81, -13.12) * mm});
            skLineSegment(sketch, "E775", {"start": v(-9.75, -13.16) * mm, "end": v(-9.74, -13.12) * mm});
            skLineSegment(sketch, "E776", {"start": v(9.74, 13.12) * mm, "end": v(9.75, 13.16) * mm});
            skLineSegment(sketch, "E777", {"start": v(-13.81, 13.12) * mm, "end": v(-13.8, 13.16) * mm});
            skLineSegment(sketch, "E778", {"start": v(3.47, -1.13) * mm, "end": v(3.52, -0.96) * mm});
            skLineSegment(sketch, "E779", {"start": v(-3.52, 0.96) * mm, "end": v(-3.47, 1.13) * mm});
            skLineSegment(sketch, "E780", {"start": v(13.81, -13.12) * mm, "end": v(13.82, -13.07) * mm});
            skLineSegment(sketch, "E781", {"start": v(-9.74, -13.12) * mm, "end": v(-9.73, -13.07) * mm});
            skLineSegment(sketch, "E782", {"start": v(9.73, 13.07) * mm, "end": v(9.74, 13.12) * mm});
            skLineSegment(sketch, "E783", {"start": v(-13.82, 13.07) * mm, "end": v(-13.81, 13.12) * mm});
            skLineSegment(sketch, "E784", {"start": v(14.93, -13.53) * mm, "end": v(14.95, -13.45) * mm});
            skLineSegment(sketch, "E785", {"start": v(9.73, -10.48) * mm, "end": v(9.74, -10.43) * mm});
            skLineSegment(sketch, "E786", {"start": v(-13.82, -10.48) * mm, "end": v(-13.81, -10.43) * mm});
            skLineSegment(sketch, "E787", {"start": v(13.81, 10.43) * mm, "end": v(13.82, 10.48) * mm});
            skLineSegment(sketch, "E788", {"start": v(-9.74, 10.43) * mm, "end": v(-9.73, 10.48) * mm});
            skLineSegment(sketch, "E789", {"start": v(-14.95, 13.45) * mm, "end": v(-14.93, 13.53) * mm});
            skLineSegment(sketch, "E790", {"start": v(3.52, -0.96) * mm, "end": v(3.56, -0.79) * mm});
            skLineSegment(sketch, "E791", {"start": v(-3.56, 0.79) * mm, "end": v(-3.52, 0.96) * mm});
            skLineSegment(sketch, "E792", {"start": v(13.82, -13.07) * mm, "end": v(13.83, -13.03) * mm});
            skLineSegment(sketch, "E793", {"start": v(-9.73, -13.07) * mm, "end": v(-9.72, -13.03) * mm});
            skLineSegment(sketch, "E794", {"start": v(9.72, -10.52) * mm, "end": v(9.73, -10.48) * mm});
            skLineSegment(sketch, "E795", {"start": v(-13.83, -10.52) * mm, "end": v(-13.82, -10.48) * mm});
            skLineSegment(sketch, "E796", {"start": v(13.82, 10.48) * mm, "end": v(13.83, 10.52) * mm});
            skLineSegment(sketch, "E797", {"start": v(-9.73, 10.48) * mm, "end": v(-9.72, 10.52) * mm});
            skLineSegment(sketch, "E798", {"start": v(9.72, 13.03) * mm, "end": v(9.73, 13.07) * mm});
            skLineSegment(sketch, "E799", {"start": v(-13.83, 13.03) * mm, "end": v(-13.82, 13.07) * mm});
            skLineSegment(sketch, "E800", {"start": v(14.95, -13.45) * mm, "end": v(14.97, -13.36) * mm});
            skLineSegment(sketch, "E801", {"start": v(-14.97, 13.36) * mm, "end": v(-14.95, 13.45) * mm});
            skLineSegment(sketch, "E802", {"start": v(3.56, -0.79) * mm, "end": v(3.6, -0.61) * mm});
            skLineSegment(sketch, "E803", {"start": v(-3.6, 0.61) * mm, "end": v(-3.56, 0.79) * mm});
            skLineSegment(sketch, "E804", {"start": v(9.7, -10.57) * mm, "end": v(9.72, -10.52) * mm});
            skLineSegment(sketch, "E805", {"start": v(-13.84, -10.57) * mm, "end": v(-13.83, -10.52) * mm});
            skLineSegment(sketch, "E806", {"start": v(13.83, 10.52) * mm, "end": v(13.84, 10.57) * mm});
            skLineSegment(sketch, "E807", {"start": v(-9.72, 10.52) * mm, "end": v(-9.7, 10.57) * mm});
            skLineSegment(sketch, "E808", {"start": v(14.97, -13.36) * mm, "end": v(14.98, -13.27) * mm});
            skLineSegment(sketch, "E809", {"start": v(-14.98, 13.27) * mm, "end": v(-14.97, 13.36) * mm});
            skLineSegment(sketch, "E810", {"start": v(13.83, -13.03) * mm, "end": v(13.84, -12.98) * mm});
            skLineSegment(sketch, "E811", {"start": v(-9.72, -13.03) * mm, "end": v(-9.7, -12.98) * mm});
            skLineSegment(sketch, "E812", {"start": v(9.7, 12.98) * mm, "end": v(9.72, 13.03) * mm});
            skLineSegment(sketch, "E813", {"start": v(-13.84, 12.98) * mm, "end": v(-13.83, 13.03) * mm});
            skLineSegment(sketch, "E814", {"start": v(3.6, -0.61) * mm, "end": v(3.62, -0.44) * mm});
            skLineSegment(sketch, "E815", {"start": v(-3.62, 0.44) * mm, "end": v(-3.6, 0.61) * mm});
            skLineSegment(sketch, "E816", {"start": v(-9.7, -12.98) * mm, "end": v(-9.7, -12.94) * mm});
            skLineSegment(sketch, "E817", {"start": v(9.7, 12.94) * mm, "end": v(9.7, 12.98) * mm});
            skLineSegment(sketch, "E818", {"start": v(9.7, -10.61) * mm, "end": v(9.7, -10.57) * mm});
            skLineSegment(sketch, "E819", {"start": v(-9.7, 10.57) * mm, "end": v(-9.7, 10.61) * mm});
            skLineSegment(sketch, "E820", {"start": v(14.98, -13.27) * mm, "end": v(15, -13.18) * mm});
            skLineSegment(sketch, "E821", {"start": v(-15, 13.18) * mm, "end": v(-14.98, 13.27) * mm});
            skLineSegment(sketch, "E822", {"start": v(13.84, -12.98) * mm, "end": v(13.85, -12.94) * mm});
            skLineSegment(sketch, "E823", {"start": v(-13.85, 12.94) * mm, "end": v(-13.84, 12.98) * mm});
            skLineSegment(sketch, "E824", {"start": v(-13.85, -10.61) * mm, "end": v(-13.84, -10.57) * mm});
            skLineSegment(sketch, "E825", {"start": v(13.84, 10.57) * mm, "end": v(13.85, 10.61) * mm});
            skLineSegment(sketch, "E826", {"start": v(3.62, -0.44) * mm, "end": v(3.64, -0.26) * mm});
            skLineSegment(sketch, "E827", {"start": v(-3.64, 0.26) * mm, "end": v(-3.62, 0.44) * mm});
            skLineSegment(sketch, "E828", {"start": v(13.85, -12.94) * mm, "end": v(13.85, -12.9) * mm});
            skLineSegment(sketch, "E829", {"start": v(-13.85, -10.66) * mm, "end": v(-13.85, -10.61) * mm});
            skLineSegment(sketch, "E830", {"start": v(13.85, 10.61) * mm, "end": v(13.85, 10.66) * mm});
            skLineSegment(sketch, "E831", {"start": v(-13.85, 12.9) * mm, "end": v(-13.85, 12.94) * mm});
            skLineSegment(sketch, "E832", {"start": v(15, -13.18) * mm, "end": v(15, -13.09) * mm});
            skLineSegment(sketch, "E833", {"start": v(-15, 13.09) * mm, "end": v(-15, 13.18) * mm});
            skLineSegment(sketch, "E834", {"start": v(-9.7, -12.94) * mm, "end": v(-9.7, -12.9) * mm});
            skLineSegment(sketch, "E835", {"start": v(9.7, -10.66) * mm, "end": v(9.7, -10.61) * mm});
            skLineSegment(sketch, "E836", {"start": v(-9.7, 10.61) * mm, "end": v(-9.7, 10.66) * mm});
            skLineSegment(sketch, "E837", {"start": v(9.7, 12.9) * mm, "end": v(9.7, 12.94) * mm});
            skLineSegment(sketch, "E838", {"start": v(3.64, -0.26) * mm, "end": v(3.65, -0.09) * mm});
            skLineSegment(sketch, "E839", {"start": v(-3.65, 0.09) * mm, "end": v(-3.64, 0.26) * mm});
            skLineSegment(sketch, "E840", {"start": v(15, -13.09) * mm, "end": v(15, -13) * mm});
            skLineSegment(sketch, "E841", {"start": v(-15, 13) * mm, "end": v(-15, 13.09) * mm});
            skLineSegment(sketch, "E842", {"start": v(13.85, -12.9) * mm, "end": v(13.85, -12.85) * mm});
            skLineSegment(sketch, "E843", {"start": v(-9.7, -12.9) * mm, "end": v(-9.7, -12.85) * mm});
            skLineSegment(sketch, "E844", {"start": v(9.7, -10.7) * mm, "end": v(9.7, -10.66) * mm});
            skLineSegment(sketch, "E845", {"start": v(-13.85, -10.7) * mm, "end": v(-13.85, -10.66) * mm});
            skLineSegment(sketch, "E846", {"start": v(13.85, 10.66) * mm, "end": v(13.85, 10.7) * mm});
            skLineSegment(sketch, "E847", {"start": v(-9.7, 10.66) * mm, "end": v(-9.7, 10.7) * mm});
            skLineSegment(sketch, "E848", {"start": v(9.7, 12.85) * mm, "end": v(9.7, 12.9) * mm});
            skLineSegment(sketch, "E849", {"start": v(-13.85, 12.85) * mm, "end": v(-13.85, 12.9) * mm});
            skLineSegment(sketch, "E850", {"start": v(12.8, -8.25) * mm, "end": v(12.8, 8.25) * mm});
            skLineSegment(sketch, "E851", {"start": v(-12.8, -8.25) * mm, "end": v(-12.8, 8.25) * mm});
            skLineSegment(sketch, "E852", {"start": v(-15, -13) * mm, "end": v(-15, 13) * mm});
            skLineSegment(sketch, "E853", {"start": v(-13.85, -12.85) * mm, "end": v(-13.85, -10.7) * mm});
            skLineSegment(sketch, "E854", {"start": v(-13.85, 10.7) * mm, "end": v(-13.85, 12.85) * mm});
            skLineSegment(sketch, "E855", {"start": v(-9.7, -12.85) * mm, "end": v(-9.7, -10.7) * mm});
            skLineSegment(sketch, "E856", {"start": v(-9.7, 10.7) * mm, "end": v(-9.7, 12.85) * mm});
            skLineSegment(sketch, "E857", {"start": v(-8.25, 10.05) * mm, "end": v(-8.25, 12.8) * mm});
            skLineSegment(sketch, "E858", {"start": v(-8.25, -12.8) * mm, "end": v(-8.25, -10.05) * mm});
            skLineSegment(sketch, "E859", {"start": v(-6, -4.2) * mm, "end": v(-6, -0.92) * mm});
            skLineSegment(sketch, "E860", {"start": v(-6, 0.92) * mm, "end": v(-6, 4.2) * mm});
            skLineSegment(sketch, "E861", {"start": v(-4.5, 14.5) * mm, "end": v(-4.5, 15) * mm});
            skLineSegment(sketch, "E862", {"start": v(-4, 12.8) * mm, "end": v(-4, 14.5) * mm});
            skLineSegment(sketch, "E863", {"start": v(-3.65, -0.09) * mm, "end": v(-3.65, 0.09) * mm});
            skLineSegment(sketch, "E864", {"start": v(3.65, -0.09) * mm, "end": v(3.65, 0.09) * mm});
            skLineSegment(sketch, "E865", {"start": v(4, 12.8) * mm, "end": v(4, 14.5) * mm});
            skLineSegment(sketch, "E866", {"start": v(4.5, 14.5) * mm, "end": v(4.5, 15) * mm});
            skLineSegment(sketch, "E867", {"start": v(6, 0.92) * mm, "end": v(6, 4.2) * mm});
            skLineSegment(sketch, "E868", {"start": v(6, -4.2) * mm, "end": v(6, -0.92) * mm});
            skLineSegment(sketch, "E869", {"start": v(8.25, 10.05) * mm, "end": v(8.25, 12.8) * mm});
            skLineSegment(sketch, "E870", {"start": v(8.25, -12.8) * mm, "end": v(8.25, -10.05) * mm});
            skLineSegment(sketch, "E871", {"start": v(9.7, 10.7) * mm, "end": v(9.7, 12.85) * mm});
            skLineSegment(sketch, "E872", {"start": v(9.7, -12.85) * mm, "end": v(9.7, -10.7) * mm});
            skLineSegment(sketch, "E873", {"start": v(13.85, 10.7) * mm, "end": v(13.85, 12.85) * mm});
            skLineSegment(sketch, "E874", {"start": v(13.85, -12.85) * mm, "end": v(13.85, -10.7) * mm});
            skLineSegment(sketch, "E875", {"start": v(15, -13) * mm, "end": v(15, 13) * mm});
            skSolve(sketch);
        }
        {
            var Q0;
            Q0=makeQuery(id+"F0.imprint","IMPRINT",FACE,{"disambiguationData":[TD([[makeQuery(id+"F0.imprint","IMPRINT",EDGE,{"derivedFrom":sQuery(id+"F0.wireOp",EDGE,"E0")}),1.0]])]});
            extrude(context, id + "F1", {"entities" : qUnion([Q0]), "depth" : 25 * mm});
        }
    });
